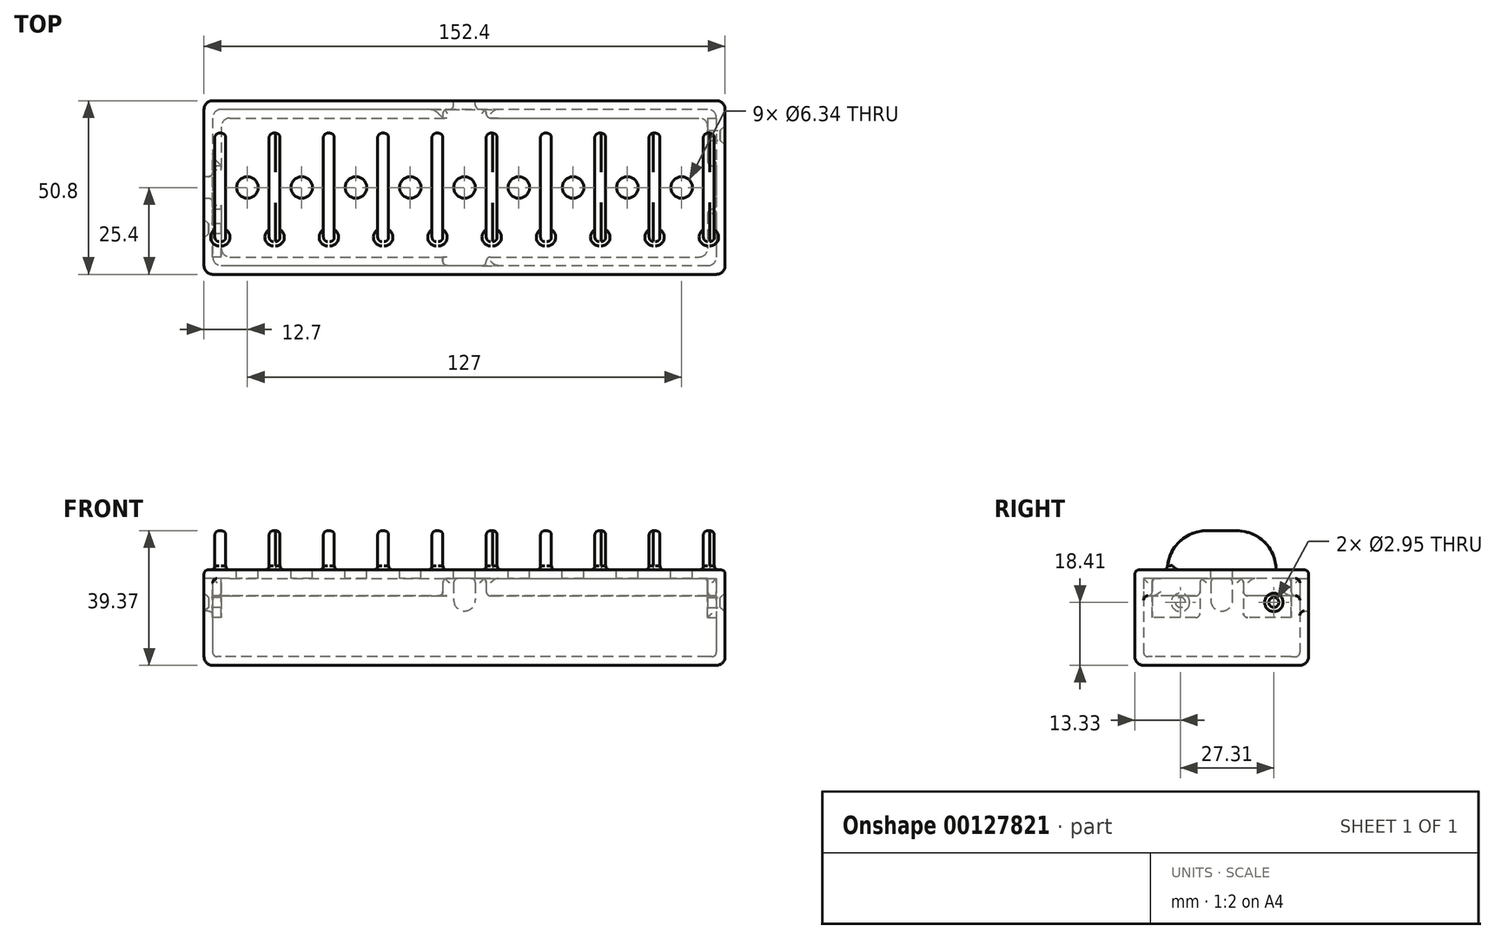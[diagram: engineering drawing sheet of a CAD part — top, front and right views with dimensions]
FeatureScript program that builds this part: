
annotation { "Feature Type Name" : "Feature", "Feature Type Description" : "" }
export const myFeature = defineFeature(function(context is Context, id is Id, definition is map)
    precondition{}
    {
        {
            var Q0;
            Q0=qCreatedBy(makeId("Top.planeOp"),FACE);
            var sketch = newSketch(context, id + "F0", { "sketchPlane" : qUnion([Q0])});
            skLineSegment(sketch, "E0.bottom", {"start": v(76.2, 25.4) * mm, "end": v(-76.2, 25.4) * mm});
            skLineSegment(sketch, "E0.top", {"start": v(76.2, -25.4) * mm, "end": v(-76.2, -25.4) * mm});
            skLineSegment(sketch, "E0.left", {"start": v(76.2, 25.4) * mm, "end": v(76.2, -25.4) * mm});
            skLineSegment(sketch, "E0.right", {"start": v(-76.2, 25.4) * mm, "end": v(-76.2, -25.4) * mm});
            skPoint(sketch, "E0.middle", {"position": v(0, 0) * mm});
            skSolve(sketch);
        }
        {
            var Q0;
            Q0=makeQuery(id+"F0.imprint","IMPRINT",FACE,{"disambiguationData":[TD([[makeQuery(id+"F0.imprint","IMPRINT",EDGE,{"derivedFrom":sQuery(id+"F0.wireOp",EDGE,"E0.bottom")}),1.0]])]});
            extrude(context, id + "F1", {"entities" : qUnion([Q0]), "depth" : 25.4 * mm});
        }
        {
            var Q0;
            Q0=makeQuery(id+"F1.opExtrude","CAP_FACE",FACE,{"disambiguationData":[OSD([sQuery(id+"F0.wireOp",EDGE,"E0.bottom"),sQuery(id+"F0.wireOp",EDGE,"E0.top"),sQuery(id+"F0.wireOp",EDGE,"E0.left"),sQuery(id+"F0.wireOp",EDGE,"E0.right")])],"isStart":false});
            shell(context, id + "F2", {"entities" : qUnion([Q0]), "thickness" : 2.54 * mm});
        }
        {
            var Q0;
            Q0=makeQuery(id+"F1.opExtrude","CAP_FACE",FACE,{"disambiguationData":[OSD([sQuery(id+"F0.wireOp",EDGE,"E0.bottom"),sQuery(id+"F0.wireOp",EDGE,"E0.top"),sQuery(id+"F0.wireOp",EDGE,"E0.left"),sQuery(id+"F0.wireOp",EDGE,"E0.right")])],"isStart":false});
            var sketch = newSketch(context, id + "F3", { "sketchPlane" : qUnion([Q0])});
            skLineSegment(sketch, "E1.bottom", {"start": v(-73.66, 22.86) * mm, "end": v(73.66, 22.86) * mm});
            skLineSegment(sketch, "E1.top", {"start": v(-73.66, -22.86) * mm, "end": v(73.66, -22.86) * mm});
            skLineSegment(sketch, "E1.left", {"start": v(-73.66, 22.86) * mm, "end": v(-73.66, -22.86) * mm});
            skLineSegment(sketch, "E1.right", {"start": v(73.66, 22.86) * mm, "end": v(73.66, -22.86) * mm});
            skLineSegment(sketch, "E2.0", {"start": v(-71.12, -20.32) * mm, "end": v(71.12, -20.32) * mm});
            skLineSegment(sketch, "E2.1", {"start": v(-71.12, 20.32) * mm, "end": v(-71.12, -20.32) * mm});
            skLineSegment(sketch, "E2.2", {"start": v(-71.12, 20.32) * mm, "end": v(71.12, 20.32) * mm});
            skLineSegment(sketch, "E2.3", {"start": v(71.12, 20.32) * mm, "end": v(71.12, -20.32) * mm});
            skSolve(sketch);
        }
        {
            var Q0;
            Q0 = qSketchRegion(id + "F3", true);
            extrude(context, id + "F4", {"entities" : qUnion([Q0]), "oppositeDirection" : true, "depth" : 5.08 * mm});
        }
        {
            var Q0;
            Q0=makeQuery(id+"F4.opExtrude","CAP_FACE",FACE,{"disambiguationData":[OSD([sQuery(id+"F3.wireOp",EDGE,"E1.bottom"),sQuery(id+"F3.wireOp",EDGE,"E1.top"),sQuery(id+"F3.wireOp",EDGE,"E1.left"),sQuery(id+"F3.wireOp",EDGE,"E1.right"),sQuery(id+"F3.wireOp",EDGE,"E2.0"),sQuery(id+"F3.wireOp",EDGE,"E2.1"),sQuery(id+"F3.wireOp",EDGE,"E2.2"),sQuery(id+"F3.wireOp",EDGE,"E2.3")])],"isStart":true});
            var sketch = newSketch(context, id + "F5", { "sketchPlane" : qUnion([Q0])});
            skLineSegment(sketch, "E3.0", {"start": v(76.2, -25.4) * mm, "end": v(-76.2, -25.4) * mm});
            skLineSegment(sketch, "E4.0", {"start": v(-76.2, 25.4) * mm, "end": v(-76.2, -25.4) * mm});
            skLineSegment(sketch, "E5.0", {"start": v(76.2, 25.4) * mm, "end": v(-76.2, 25.4) * mm});
            skLineSegment(sketch, "E6.0", {"start": v(76.2, 25.4) * mm, "end": v(76.2, -25.4) * mm});
            skSolve(sketch);
        }
        {
            var Q0;
            Q0 = qSketchRegion(id + "F5", true);
            extrude(context, id + "F6", {"entities" : qUnion([Q0]), "operationType" : NewBodyOperationType.ADD, "depth" : 2.54 * mm});
        }
        {
            var Q0;
            Q0=makeQuery(id+"F1.opExtrude","SWEPT_FACE",FACE,{"disambiguationData":[OSD([sQuery(id+"F0.wireOp",EDGE,"E0.bottom")])]});
            var sketch = newSketch(context, id + "F7", { "sketchPlane" : qUnion([Q0])});
            skLineSegment(sketch, "E7", {"start": v(-3.17, 25.4) * mm, "end": v(-3.17, 19.05) * mm});
            skLineSegment(sketch, "E8", {"start": v(-3.17, 25.4) * mm, "end": v(3.17, 25.4) * mm});
            skLineSegment(sketch, "E9", {"start": v(3.17, 25.4) * mm, "end": v(3.17, 19.05) * mm});
            skArc(sketch, "E10", {"start": v(-3.17, 19.05) * mm, "mid": v(0, 15.88) * mm, "end": v(3.17, 19.05) * mm});
            skSolve(sketch);
        }
        {
            var Q0;
            Q0=makeQuery(id+"F7.imprint","IMPRINT",FACE,{"disambiguationData":[TD([[makeQuery(id+"F7.imprint","IMPRINT",EDGE,{"derivedFrom":sQuery(id+"F7.wireOp",EDGE,"E7")}),1.0]])]});
            var Q1;
            Q1=makeQuery(id+"F2.opShell","OFFSET_FACE",FACE,{"disambiguationData":[OSD([sQuery(id+"F0.wireOp",EDGE,"E0.bottom")])]});
            extrude(context, id + "F8", {"entities" : qUnion([Q0]), "operationType" : NewBodyOperationType.REMOVE, "endBound" : BoundingType.UP_TO_SURFACE, "oppositeDirection" : true, "endBoundEntityFace" : qUnion([Q1]), "depth" : 6.35 * mm});
        }
        {
            var Q0;
            Q0=makeQuery(id+"F1.opExtrude","SWEPT_FACE",FACE,{"disambiguationData":[OSD([sQuery(id+"F0.wireOp",EDGE,"E0.right")])]});
            var sketch = newSketch(context, id + "F9", { "sketchPlane" : qUnion([Q0])});
            skLineSegment(sketch, "E11", {"start": v(-3.17, 19.05) * mm, "end": v(-3.17, 25.4) * mm});
            skLineSegment(sketch, "E12", {"start": v(-3.17, 25.4) * mm, "end": v(3.18, 25.4) * mm});
            skLineSegment(sketch, "E13", {"start": v(3.18, 25.4) * mm, "end": v(3.18, 19.05) * mm});
            skArc(sketch, "E14", {"start": v(-3.17, 19.05) * mm, "mid": v(0, 15.87) * mm, "end": v(3.18, 19.05) * mm});
            skSolve(sketch);
        }
        {
            var Q0;
            Q0=makeQuery(id+"F9.imprint","IMPRINT",FACE,{"disambiguationData":[TD([[makeQuery(id+"F9.imprint","IMPRINT",EDGE,{"derivedFrom":sQuery(id+"F9.wireOp",EDGE,"E11")}),-1.0]])]});
            var Q1;
            Q1=makeQuery(id+"F2.opShell","OFFSET_FACE",FACE,{"disambiguationData":[OSD([sQuery(id+"F0.wireOp",EDGE,"E0.right")])]});
            extrude(context, id + "F10", {"entities" : qUnion([Q0]), "operationType" : NewBodyOperationType.REMOVE, "endBound" : BoundingType.UP_TO_SURFACE, "oppositeDirection" : true, "endBoundEntityFace" : qUnion([Q1]), "depth" : 25.4 * mm});
        }
        {
            var Q0;
            Q0=makeQuery(id+"F4.opExtrude","CAP_FACE",FACE,{"disambiguationData":[OSD([sQuery(id+"F3.wireOp",EDGE,"E1.bottom"),sQuery(id+"F3.wireOp",EDGE,"E1.top"),sQuery(id+"F3.wireOp",EDGE,"E1.left"),sQuery(id+"F3.wireOp",EDGE,"E1.right"),sQuery(id+"F3.wireOp",EDGE,"E2.0"),sQuery(id+"F3.wireOp",EDGE,"E2.1"),sQuery(id+"F3.wireOp",EDGE,"E2.2"),sQuery(id+"F3.wireOp",EDGE,"E2.3")])],"isStart":false});
            var sketch = newSketch(context, id + "F11", { "sketchPlane" : qUnion([Q0])});
            skLineSegment(sketch, "E15.bottom", {"start": v(71.12, -6.35) * mm, "end": v(73.66, -6.35) * mm});
            skLineSegment(sketch, "E15.top", {"start": v(71.12, 6.35) * mm, "end": v(73.66, 6.35) * mm});
            skLineSegment(sketch, "E15.left", {"start": v(71.12, -6.35) * mm, "end": v(71.12, 6.35) * mm});
            skLineSegment(sketch, "E15.right", {"start": v(73.66, -6.35) * mm, "end": v(73.66, 6.35) * mm});
            skLineSegment(sketch, "E16.bottom", {"start": v(-6.35, 20.32) * mm, "end": v(6.35, 20.32) * mm});
            skLineSegment(sketch, "E16.top", {"start": v(-6.35, 22.86) * mm, "end": v(6.35, 22.86) * mm});
            skLineSegment(sketch, "E16.left", {"start": v(-6.35, 20.32) * mm, "end": v(-6.35, 22.86) * mm});
            skLineSegment(sketch, "E16.right", {"start": v(6.35, 20.32) * mm, "end": v(6.35, 22.86) * mm});
            skLineSegment(sketch, "E17.bottom", {"start": v(-71.12, -6.35) * mm, "end": v(-73.66, -6.35) * mm});
            skLineSegment(sketch, "E17.top", {"start": v(-71.12, 6.35) * mm, "end": v(-73.66, 6.35) * mm});
            skLineSegment(sketch, "E17.left", {"start": v(-71.12, -6.35) * mm, "end": v(-71.12, 6.35) * mm});
            skLineSegment(sketch, "E17.right", {"start": v(-73.66, -6.35) * mm, "end": v(-73.66, 6.35) * mm});
            skLineSegment(sketch, "E18.bottom", {"start": v(6.35, -22.86) * mm, "end": v(-6.35, -22.86) * mm});
            skLineSegment(sketch, "E18.top", {"start": v(6.35, -20.32) * mm, "end": v(-6.35, -20.32) * mm});
            skLineSegment(sketch, "E18.left", {"start": v(6.35, -22.86) * mm, "end": v(6.35, -20.32) * mm});
            skLineSegment(sketch, "E18.right", {"start": v(-6.35, -22.86) * mm, "end": v(-6.35, -20.32) * mm});
            skSolve(sketch);
        }
        {
            var Q0;
            Q0=makeQuery(id+"F11.imprint","IMPRINT",FACE,{"disambiguationData":[TD([[makeQuery(id+"F11.imprint","IMPRINT",EDGE,{"derivedFrom":sQuery(id+"F11.wireOp",EDGE,"E18.bottom")}),-1.0]])]});
            var Q1;
            Q1=makeQuery(id+"F11.imprint","IMPRINT",FACE,{"disambiguationData":[TD([[makeQuery(id+"F11.imprint","IMPRINT",EDGE,{"derivedFrom":sQuery(id+"F11.wireOp",EDGE,"E16.bottom")}),1.0]])]});
            var Q2;
            Q2=makeQuery(id+"F11.imprint","IMPRINT",FACE,{"disambiguationData":[TD([[makeQuery(id+"F11.imprint","IMPRINT",EDGE,{"derivedFrom":sQuery(id+"F11.wireOp",EDGE,"E15.bottom")}),1.0]])]});
            var Q3;
            Q3=makeQuery(id+"F11.imprint","IMPRINT",FACE,{"disambiguationData":[TD([[makeQuery(id+"F11.imprint","IMPRINT",EDGE,{"derivedFrom":sQuery(id+"F11.wireOp",EDGE,"E17.bottom")}),-1.0]])]});
            var Q4;
            {var subQ0=sQuery(id+"F5.wireOp",EDGE,"E5.0");var subQ1=sQuery(id+"F5.wireOp",EDGE,"E3.0");var subQ2=sQuery(id+"F5.wireOp",EDGE,"E4.0");var subQ3=sQuery(id+"F5.wireOp",EDGE,"E6.0");Q4=makeQuery(id+"F6.boolean.opBoolean","SPLIT",FACE,{"disambiguationData":[TD([makeQuery(id+"F4.opExtrude","SWEPT_FACE",FACE,{"disambiguationData":[OSD([sQuery(id+"F3.wireOp",EDGE,"E1.bottom")])]})])],"derivedFrom":makeQuery(id+"F6.opExtrude","CAP_FACE",FACE,{"disambiguationData":[OSD([subQ1,subQ2,subQ0,subQ3])],"isStart":true})});}
            extrude(context, id + "F12", {"entities" : qUnion([Q0, Q1, Q2, Q3]), "operationType" : NewBodyOperationType.REMOVE, "endBound" : BoundingType.UP_TO_SURFACE, "oppositeDirection" : true, "endBoundEntityFace" : qUnion([Q4]), "depth" : 25.4 * mm});
        }
        {
            var Q0;
            Q0=makeQuery(id+"F1.opExtrude","SWEPT_EDGE",EDGE,{"disambiguationData":[OSD([sQuery(id+"F0.wireOp",EDGE,"E0.bottom"),sQuery(id+"F0.wireOp",EDGE,"E0.right")])]});
            var Q1;
            Q1=makeQuery(id+"F1.opExtrude","SWEPT_EDGE",EDGE,{"disambiguationData":[OSD([sQuery(id+"F0.wireOp",EDGE,"E0.top"),sQuery(id+"F0.wireOp",EDGE,"E0.right")])]});
            var Q2;
            Q2=makeQuery(id+"F1.opExtrude","SWEPT_EDGE",EDGE,{"disambiguationData":[OSD([sQuery(id+"F0.wireOp",EDGE,"E0.top"),sQuery(id+"F0.wireOp",EDGE,"E0.left")])]});
            var Q3;
            Q3=makeQuery(id+"F1.opExtrude","SWEPT_EDGE",EDGE,{"disambiguationData":[OSD([sQuery(id+"F0.wireOp",EDGE,"E0.bottom"),sQuery(id+"F0.wireOp",EDGE,"E0.left")])]});
            var Q4;
            Q4=makeQuery(id+"F2.opShell","OFFSET_EDGE",EDGE,{"disambiguationData":[OSD([sQuery(id+"F0.wireOp",EDGE,"E0.top"),sQuery(id+"F0.wireOp",EDGE,"E0.left")])]});
            var Q5;
            Q5=makeQuery(id+"F2.opShell","OFFSET_EDGE",EDGE,{"disambiguationData":[OSD([sQuery(id+"F0.wireOp",EDGE,"E0.bottom"),sQuery(id+"F0.wireOp",EDGE,"E0.left")])]});
            var Q6;
            Q6=makeQuery(id+"F2.opShell","OFFSET_EDGE",EDGE,{"disambiguationData":[OSD([sQuery(id+"F0.wireOp",EDGE,"E0.top"),sQuery(id+"F0.wireOp",EDGE,"E0.right")])]});
            var Q7;
            Q7=makeQuery(id+"F2.opShell","OFFSET_EDGE",EDGE,{"disambiguationData":[OSD([sQuery(id+"F0.wireOp",EDGE,"E0.bottom"),sQuery(id+"F0.wireOp",EDGE,"E0.right")])]});
            fillet(context, id + "F13", {"entities" : qUnion([Q0, Q1, Q2, Q3, Q4, Q5, Q6, Q7]), "radius" : 2.54 * mm, "tangentPropagation" : true, "allowEdgeOverflow" : false});
        }
        {
            var Q0;
            Q0=makeQuery(id+"F6.opExtrude","SWEPT_EDGE",EDGE,{"disambiguationData":[OSD([sQuery(id+"F5.wireOp",EDGE,"E5.0"),sQuery(id+"F5.wireOp",EDGE,"E6.0")])]});
            var Q1;
            Q1=makeQuery(id+"F6.opExtrude","SWEPT_EDGE",EDGE,{"disambiguationData":[OSD([sQuery(id+"F5.wireOp",EDGE,"E3.0"),sQuery(id+"F5.wireOp",EDGE,"E6.0")])]});
            var Q2;
            Q2=makeQuery(id+"F4.opExtrude","SWEPT_EDGE",EDGE,{"disambiguationData":[OSD([sQuery(id+"F3.wireOp",EDGE,"E1.bottom"),sQuery(id+"F3.wireOp",EDGE,"E1.right")])]});
            var Q3;
            Q3=makeQuery(id+"F4.opExtrude","SWEPT_EDGE",EDGE,{"disambiguationData":[OSD([sQuery(id+"F3.wireOp",EDGE,"E1.top"),sQuery(id+"F3.wireOp",EDGE,"E1.right")])]});
            var Q4;
            Q4=makeQuery(id+"F4.opExtrude","SWEPT_EDGE",EDGE,{"disambiguationData":[OSD([sQuery(id+"F3.wireOp",EDGE,"E2.2"),sQuery(id+"F3.wireOp",EDGE,"E2.3")])]});
            var Q5;
            Q5=makeQuery(id+"F4.opExtrude","SWEPT_EDGE",EDGE,{"disambiguationData":[OSD([sQuery(id+"F3.wireOp",EDGE,"E2.0"),sQuery(id+"F3.wireOp",EDGE,"E2.3")])]});
            var Q6;
            Q6=makeQuery(id+"F4.opExtrude","SWEPT_EDGE",EDGE,{"disambiguationData":[OSD([sQuery(id+"F3.wireOp",EDGE,"E1.bottom"),sQuery(id+"F3.wireOp",EDGE,"E1.left")])]});
            var Q7;
            Q7=makeQuery(id+"F6.opExtrude","SWEPT_EDGE",EDGE,{"disambiguationData":[OSD([sQuery(id+"F5.wireOp",EDGE,"E4.0"),sQuery(id+"F5.wireOp",EDGE,"E5.0")])]});
            var Q8;
            Q8=makeQuery(id+"F6.opExtrude","SWEPT_EDGE",EDGE,{"disambiguationData":[OSD([sQuery(id+"F5.wireOp",EDGE,"E3.0"),sQuery(id+"F5.wireOp",EDGE,"E4.0")])]});
            var Q9;
            Q9=makeQuery(id+"F4.opExtrude","SWEPT_EDGE",EDGE,{"disambiguationData":[OSD([sQuery(id+"F3.wireOp",EDGE,"E1.top"),sQuery(id+"F3.wireOp",EDGE,"E1.left")])]});
            var Q10;
            Q10=makeQuery(id+"F4.opExtrude","SWEPT_EDGE",EDGE,{"disambiguationData":[OSD([sQuery(id+"F3.wireOp",EDGE,"E2.0"),sQuery(id+"F3.wireOp",EDGE,"E2.1")])]});
            var Q11;
            Q11=makeQuery(id+"F4.opExtrude","SWEPT_EDGE",EDGE,{"disambiguationData":[OSD([sQuery(id+"F3.wireOp",EDGE,"E2.1"),sQuery(id+"F3.wireOp",EDGE,"E2.2")])]});
            fillet(context, id + "F14", {"entities" : qUnion([Q0, Q1, Q2, Q3, Q4, Q5, Q6, Q7, Q8, Q9, Q10, Q11]), "radius" : 2.54 * mm, "tangentPropagation" : true, "allowEdgeOverflow" : false});
        }
        {
            var Q0;
            Q0=makeQuery(id+"F1.opExtrude","CAP_FACE",FACE,{"disambiguationData":[OSD([sQuery(id+"F0.wireOp",EDGE,"E0.bottom"),sQuery(id+"F0.wireOp",EDGE,"E0.top"),sQuery(id+"F0.wireOp",EDGE,"E0.left"),sQuery(id+"F0.wireOp",EDGE,"E0.right")])],"isStart":true});
            fillet(context, id + "F15", {"entities" : qUnion([Q0]), "radius" : 2.54 * mm, "tangentPropagation" : true, "allowEdgeOverflow" : false});
        }
        {
            var Q0;
            Q0=makeQuery(id+"F6.opExtrude","CAP_FACE",FACE,{"disambiguationData":[OSD([sQuery(id+"F5.wireOp",EDGE,"E3.0"),sQuery(id+"F5.wireOp",EDGE,"E4.0"),sQuery(id+"F5.wireOp",EDGE,"E5.0"),sQuery(id+"F5.wireOp",EDGE,"E6.0")])],"isStart":false});
            var sketch = newSketch(context, id + "F16", { "sketchPlane" : qUnion([Q0])});
            skCircle(sketch, "E19", {"center": v(63.5, 0) * mm, "radius": 3.17 * mm});
            skCircle(sketch, "E20.1.0.0", {"center": v(47.62, 0) * mm, "radius": 3.17 * mm});
            skCircle(sketch, "E20.2.0.0", {"center": v(31.75, 0) * mm, "radius": 3.17 * mm});
            skCircle(sketch, "E20.3.0.0", {"center": v(15.88, 0) * mm, "radius": 3.17 * mm});
            skCircle(sketch, "E20.4.0.0", {"center": v(0, 0) * mm, "radius": 3.17 * mm});
            skCircle(sketch, "E20.5.0.0", {"center": v(-15.87, 0) * mm, "radius": 3.17 * mm});
            skLineSegment(sketch, "E20.direction1", {"start": v(63.5, 0) * mm, "end": v(47.62, 0) * mm, "construction": true});
            skCircle(sketch, "E21.0.6.0", {"center": v(-31.75, 0) * mm, "radius": 3.17 * mm});
            skCircle(sketch, "E21.0.7.0", {"center": v(-47.62, 0) * mm, "radius": 3.17 * mm});
            skCircle(sketch, "E22.0.8.0", {"center": v(-63.5, 0) * mm, "radius": 3.17 * mm});
            skSolve(sketch);
        }
        {
            var Q0;
            Q0 = qSketchRegion(id + "F16", true);
            var Q1;
            {var subQ0=sQuery(id+"F5.wireOp",EDGE,"E6.0");var subQ1=sQuery(id+"F5.wireOp",EDGE,"E5.0");var subQ2=sQuery(id+"F5.wireOp",EDGE,"E4.0");var subQ3=sQuery(id+"F5.wireOp",EDGE,"E3.0");var subQ4=makeQuery(id+"F6.opExtrude","CAP_FACE",FACE,{"disambiguationData":[OSD([subQ3,subQ2,subQ1,subQ0])],"isStart":true});Q1=makeQuery(id+"F12.boolean.opBoolean","MERGE",FACE,{"derivedFrom":[makeQuery(id+"F6.boolean.opBoolean","SPLIT",FACE,{"disambiguationData":[TD([makeQuery(id+"F4.opExtrude","SWEPT_FACE",FACE,{"disambiguationData":[OSD([sQuery(id+"F3.wireOp",EDGE,"E1.bottom")])]})])],"derivedFrom":subQ4}),makeQuery(id+"F6.boolean.opBoolean","SPLIT",FACE,{"disambiguationData":[TD([makeQuery(id+"F4.opExtrude","SWEPT_FACE",FACE,{"disambiguationData":[OSD([sQuery(id+"F3.wireOp",EDGE,"E2.0")])]})])],"derivedFrom":subQ4})],"fromTools":[makeQuery(id+"F12.opExtrude","CAP_FACE",FACE,{"disambiguationData":[OSD([sQuery(id+"F11.wireOp",EDGE,"E15.bottom"),sQuery(id+"F11.wireOp",EDGE,"E15.top"),sQuery(id+"F11.wireOp",EDGE,"E15.left"),sQuery(id+"F11.wireOp",EDGE,"E15.right")])],"isStart":false}),makeQuery(id+"F12.opExtrude","CAP_FACE",FACE,{"disambiguationData":[OSD([sQuery(id+"F11.wireOp",EDGE,"E16.bottom"),sQuery(id+"F11.wireOp",EDGE,"E16.top"),sQuery(id+"F11.wireOp",EDGE,"E16.left"),sQuery(id+"F11.wireOp",EDGE,"E16.right")])],"isStart":false}),makeQuery(id+"F12.opExtrude","CAP_FACE",FACE,{"disambiguationData":[OSD([sQuery(id+"F11.wireOp",EDGE,"E17.bottom"),sQuery(id+"F11.wireOp",EDGE,"E17.top"),sQuery(id+"F11.wireOp",EDGE,"E17.left"),sQuery(id+"F11.wireOp",EDGE,"E17.right")])],"isStart":false}),makeQuery(id+"F12.opExtrude","CAP_FACE",FACE,{"disambiguationData":[OSD([sQuery(id+"F11.wireOp",EDGE,"E18.bottom"),sQuery(id+"F11.wireOp",EDGE,"E18.top"),sQuery(id+"F11.wireOp",EDGE,"E18.left"),sQuery(id+"F11.wireOp",EDGE,"E18.right")])],"isStart":false})]});}
            extrude(context, id + "F17", {"entities" : qUnion([Q0]), "operationType" : NewBodyOperationType.REMOVE, "endBound" : BoundingType.UP_TO_SURFACE, "oppositeDirection" : true, "endBoundEntityFace" : qUnion([Q1]), "depth" : 25.4 * mm});
        }
        {
            var Q0;
            {var subQ0=sQuery(id+"F3.wireOp",EDGE,"E2.3");var subQ1=sQuery(id+"F3.wireOp",EDGE,"E2.2");var subQ2=sQuery(id+"F3.wireOp",EDGE,"E1.right");var subQ3=sQuery(id+"F3.wireOp",EDGE,"E1.bottom");Q0=makeQuery(id+"F12.boolean.opBoolean","SPLIT",FACE,{"disambiguationData":[TD([makeQuery(id+"F12.opExtrude","SWEPT_FACE",FACE,{"disambiguationData":[OSD([sQuery(id+"F11.wireOp",EDGE,"E15.bottom")])]})])],"derivedFrom":makeQuery(id+"F4.opExtrude","CAP_FACE",FACE,{"disambiguationData":[OSD([subQ3,sQuery(id+"F3.wireOp",EDGE,"E1.top"),sQuery(id+"F3.wireOp",EDGE,"E1.left"),subQ2,sQuery(id+"F3.wireOp",EDGE,"E2.0"),sQuery(id+"F3.wireOp",EDGE,"E2.1"),subQ1,subQ0])],"isStart":false})});}
            var sketch = newSketch(context, id + "F18", { "sketchPlane" : qUnion([Q0])});
            skLineSegment(sketch, "E23.bottom", {"start": v(73.66, -6.35) * mm, "end": v(71.12, -6.35) * mm});
            skLineSegment(sketch, "E23.left", {"start": v(73.66, -6.35) * mm, "end": v(73.66, -20.32) * mm});
            skLineSegment(sketch, "E24.top", {"start": v(-71.12, 6.35) * mm, "end": v(-73.66, 6.35) * mm});
            skLineSegment(sketch, "E24.right", {"start": v(-73.66, 20.32) * mm, "end": v(-73.66, 6.35) * mm});
            skLineSegment(sketch, "E25", {"start": v(71.12, -6.35) * mm, "end": v(71.12, -20.32) * mm});
            skLineSegment(sketch, "E26", {"start": v(71.12, -20.32) * mm, "end": v(73.66, -20.32) * mm});
            skLineSegment(sketch, "E27", {"start": v(-71.12, 6.35) * mm, "end": v(-71.12, 20.32) * mm});
            skLineSegment(sketch, "E28", {"start": v(-71.12, 20.32) * mm, "end": v(-73.66, 20.32) * mm});
            skSolve(sketch);
        }
        {
            var Q0;
            Q0=makeQuery(id+"F18.imprint","IMPRINT",FACE,{"disambiguationData":[TD([[makeQuery(id+"F18.imprint","IMPRINT",EDGE,{"derivedFrom":sQuery(id+"F18.wireOp",EDGE,"E23.bottom")}),-1.0]])]});
            var Q1;
            Q1=makeQuery(id+"F18.imprint","IMPRINT",FACE,{"disambiguationData":[TD([[makeQuery(id+"F18.imprint","IMPRINT",EDGE,{"derivedFrom":sQuery(id+"F18.wireOp",EDGE,"E24.bottom")}),1.0]])]});
            var Q2;
            Q2=makeQuery(id+"F18.imprint","IMPRINT",FACE,{"disambiguationData":[TD([[makeQuery(id+"F18.imprint","IMPRINT",EDGE,{"derivedFrom":sQuery(id+"F18.wireOp",EDGE,"E24.top")}),-1.0]])]});
            extrude(context, id + "F19", {"entities" : qUnion([Q0, Q1, Q2]), "operationType" : NewBodyOperationType.ADD, "depth" : 6.35 * mm});
        }
        {
            var Q0;
            Q0=makeQuery(id+"F6.opExtrude","CAP_EDGE",EDGE,{"disambiguationData":[OSD([sQuery(id+"F5.wireOp",EDGE,"E6.0")])],"isStart":false});
            var Q1;
            Q1=makeQuery(id+"F6.opExtrude","CAP_EDGE",EDGE,{"disambiguationData":[OSD([sQuery(id+"F5.wireOp",EDGE,"E6.0")])],"isStart":true});
            var Q2;
            Q2=makeQuery(id+"F17.boolean.opBoolean","COPY",EDGE,{"derivedFrom":makeQuery(id+"F17.opExtrude","CAP_EDGE",EDGE,{"disambiguationData":[OSD([sQuery(id+"F16.wireOp",EDGE,"E19")])],"isStart":true})});
            var Q3;
            Q3=makeQuery(id+"F17.boolean.opBoolean","COPY",EDGE,{"derivedFrom":makeQuery(id+"F17.opExtrude","CAP_EDGE",EDGE,{"disambiguationData":[OSD([sQuery(id+"F16.wireOp",EDGE,"E20.1.0.0")])],"isStart":true})});
            var Q4;
            Q4=makeQuery(id+"F17.boolean.opBoolean","COPY",EDGE,{"derivedFrom":makeQuery(id+"F17.opExtrude","CAP_EDGE",EDGE,{"disambiguationData":[OSD([sQuery(id+"F16.wireOp",EDGE,"E20.2.0.0")])],"isStart":true})});
            var Q5;
            Q5=makeQuery(id+"F17.boolean.opBoolean","COPY",EDGE,{"derivedFrom":makeQuery(id+"F17.opExtrude","CAP_EDGE",EDGE,{"disambiguationData":[OSD([sQuery(id+"F16.wireOp",EDGE,"E20.3.0.0")])],"isStart":true})});
            var Q6;
            Q6=makeQuery(id+"F17.boolean.opBoolean","COPY",EDGE,{"derivedFrom":makeQuery(id+"F17.opExtrude","CAP_EDGE",EDGE,{"disambiguationData":[OSD([sQuery(id+"F16.wireOp",EDGE,"E20.4.0.0")])],"isStart":true})});
            var Q7;
            Q7=makeQuery(id+"F17.boolean.opBoolean","COPY",EDGE,{"derivedFrom":makeQuery(id+"F17.opExtrude","CAP_EDGE",EDGE,{"disambiguationData":[OSD([sQuery(id+"F16.wireOp",EDGE,"E20.5.0.0")])],"isStart":true})});
            var Q8;
            Q8=makeQuery(id+"F17.boolean.opBoolean","COPY",EDGE,{"derivedFrom":makeQuery(id+"F17.opExtrude","CAP_EDGE",EDGE,{"disambiguationData":[OSD([sQuery(id+"F16.wireOp",EDGE,"E21.0.6.0")])],"isStart":true})});
            var Q9;
            Q9=makeQuery(id+"F17.boolean.opBoolean","COPY",EDGE,{"derivedFrom":makeQuery(id+"F17.opExtrude","CAP_EDGE",EDGE,{"disambiguationData":[OSD([sQuery(id+"F16.wireOp",EDGE,"E21.0.7.0")])],"isStart":true})});
            var Q10;
            Q10=makeQuery(id+"F17.boolean.opBoolean","COPY",EDGE,{"derivedFrom":makeQuery(id+"F17.opExtrude","CAP_EDGE",EDGE,{"disambiguationData":[OSD([sQuery(id+"F16.wireOp",EDGE,"E22.0.8.0")])],"isStart":true})});
            var Q11;
            {var subQ0=sQuery(id+"F5.wireOp",EDGE,"E6.0");var subQ1=sQuery(id+"F5.wireOp",EDGE,"E5.0");var subQ2=sQuery(id+"F5.wireOp",EDGE,"E4.0");var subQ3=sQuery(id+"F5.wireOp",EDGE,"E3.0");var subQ4=makeQuery(id+"F6.opExtrude","CAP_FACE",FACE,{"disambiguationData":[OSD([subQ3,subQ2,subQ1,subQ0])],"isStart":true});var subQ5=sQuery(id+"F3.wireOp",EDGE,"E1.top");var subQ6=sQuery(id+"F3.wireOp",EDGE,"E1.right");Q11=makeQuery(id+"F14.opFillet","BLEND_EDGE",EDGE,{"blendedFrom":[makeQuery(id+"F4.opExtrude","SWEPT_EDGE",EDGE,{"disambiguationData":[OSD([subQ5,subQ6])]}),makeQuery(id+"F12.boolean.opBoolean","MERGE",FACE,{"derivedFrom":[makeQuery(id+"F6.boolean.opBoolean","SPLIT",FACE,{"disambiguationData":[TD([makeQuery(id+"F4.opExtrude","SWEPT_FACE",FACE,{"disambiguationData":[OSD([sQuery(id+"F3.wireOp",EDGE,"E1.bottom")])]})])],"derivedFrom":subQ4}),makeQuery(id+"F6.boolean.opBoolean","SPLIT",FACE,{"disambiguationData":[TD([makeQuery(id+"F4.opExtrude","SWEPT_FACE",FACE,{"disambiguationData":[OSD([sQuery(id+"F3.wireOp",EDGE,"E2.0")])]})])],"derivedFrom":subQ4})],"fromTools":[makeQuery(id+"F12.opExtrude","CAP_FACE",FACE,{"disambiguationData":[OSD([sQuery(id+"F11.wireOp",EDGE,"E15.bottom"),sQuery(id+"F11.wireOp",EDGE,"E15.top"),sQuery(id+"F11.wireOp",EDGE,"E15.left"),sQuery(id+"F11.wireOp",EDGE,"E15.right")])],"isStart":false}),makeQuery(id+"F12.opExtrude","CAP_FACE",FACE,{"disambiguationData":[OSD([sQuery(id+"F11.wireOp",EDGE,"E16.bottom"),sQuery(id+"F11.wireOp",EDGE,"E16.top"),sQuery(id+"F11.wireOp",EDGE,"E16.left"),sQuery(id+"F11.wireOp",EDGE,"E16.right")])],"isStart":false}),makeQuery(id+"F12.opExtrude","CAP_FACE",FACE,{"disambiguationData":[OSD([sQuery(id+"F11.wireOp",EDGE,"E17.bottom"),sQuery(id+"F11.wireOp",EDGE,"E17.top"),sQuery(id+"F11.wireOp",EDGE,"E17.left"),sQuery(id+"F11.wireOp",EDGE,"E17.right")])],"isStart":false}),makeQuery(id+"F12.opExtrude","CAP_FACE",FACE,{"disambiguationData":[OSD([sQuery(id+"F11.wireOp",EDGE,"E18.bottom"),sQuery(id+"F11.wireOp",EDGE,"E18.top"),sQuery(id+"F11.wireOp",EDGE,"E18.left"),sQuery(id+"F11.wireOp",EDGE,"E18.right")])],"isStart":false})]})],"blendedInto":[makeQuery(id+"F12.boolean.opBoolean","MERGE",FACE,{"derivedFrom":[makeQuery(id+"F6.boolean.opBoolean","SPLIT",FACE,{"disambiguationData":[TD([makeQuery(id+"F4.opExtrude","SWEPT_FACE",FACE,{"disambiguationData":[OSD([sQuery(id+"F3.wireOp",EDGE,"E1.bottom")])]})])],"derivedFrom":subQ4}),makeQuery(id+"F6.boolean.opBoolean","SPLIT",FACE,{"disambiguationData":[TD([makeQuery(id+"F4.opExtrude","SWEPT_FACE",FACE,{"disambiguationData":[OSD([sQuery(id+"F3.wireOp",EDGE,"E2.0")])]})])],"derivedFrom":subQ4})],"fromTools":[makeQuery(id+"F12.opExtrude","CAP_FACE",FACE,{"disambiguationData":[OSD([sQuery(id+"F11.wireOp",EDGE,"E15.bottom"),sQuery(id+"F11.wireOp",EDGE,"E15.top"),sQuery(id+"F11.wireOp",EDGE,"E15.left"),sQuery(id+"F11.wireOp",EDGE,"E15.right")])],"isStart":false}),makeQuery(id+"F12.opExtrude","CAP_FACE",FACE,{"disambiguationData":[OSD([sQuery(id+"F11.wireOp",EDGE,"E16.bottom"),sQuery(id+"F11.wireOp",EDGE,"E16.top"),sQuery(id+"F11.wireOp",EDGE,"E16.left"),sQuery(id+"F11.wireOp",EDGE,"E16.right")])],"isStart":false}),makeQuery(id+"F12.opExtrude","CAP_FACE",FACE,{"disambiguationData":[OSD([sQuery(id+"F11.wireOp",EDGE,"E17.bottom"),sQuery(id+"F11.wireOp",EDGE,"E17.top"),sQuery(id+"F11.wireOp",EDGE,"E17.left"),sQuery(id+"F11.wireOp",EDGE,"E17.right")])],"isStart":false}),makeQuery(id+"F12.opExtrude","CAP_FACE",FACE,{"disambiguationData":[OSD([sQuery(id+"F11.wireOp",EDGE,"E18.bottom"),sQuery(id+"F11.wireOp",EDGE,"E18.top"),sQuery(id+"F11.wireOp",EDGE,"E18.left"),sQuery(id+"F11.wireOp",EDGE,"E18.right")])],"isStart":false})]})]});}
            var Q12;
            {var subQ0=sQuery(id+"F3.wireOp",EDGE,"E1.right");var subQ1=sQuery(id+"F3.wireOp",EDGE,"E1.top");Q12=makeQuery(id+"F12.boolean.opBoolean","SPLIT",EDGE,{"disambiguationData":[TD([makeQuery(id+"F4.opExtrude","SWEPT_FACE",FACE,{"disambiguationData":[OSD([subQ1])]})])],"derivedFrom":makeQuery(id+"F4.opExtrude","CAP_EDGE",EDGE,{"disambiguationData":[OSD([subQ0])],"isStart":false})});}
            var Q13;
            {var subQ0=sQuery(id+"F3.wireOp",EDGE,"E2.3");var subQ1=sQuery(id+"F3.wireOp",EDGE,"E2.0");Q13=makeQuery(id+"F12.boolean.opBoolean","SPLIT",EDGE,{"disambiguationData":[TD([makeQuery(id+"F4.opExtrude","SWEPT_FACE",FACE,{"disambiguationData":[OSD([subQ1])]})])],"derivedFrom":makeQuery(id+"F4.opExtrude","CAP_EDGE",EDGE,{"disambiguationData":[OSD([subQ0])],"isStart":false})});}
            var Q14;
            {var subQ0=sQuery(id+"F3.wireOp",EDGE,"E2.0");var subQ1=sQuery(id+"F3.wireOp",EDGE,"E2.3");var subQ2=sQuery(id+"F5.wireOp",EDGE,"E6.0");var subQ3=sQuery(id+"F5.wireOp",EDGE,"E5.0");var subQ4=sQuery(id+"F5.wireOp",EDGE,"E4.0");var subQ5=sQuery(id+"F5.wireOp",EDGE,"E3.0");var subQ6=makeQuery(id+"F6.opExtrude","CAP_FACE",FACE,{"disambiguationData":[OSD([subQ5,subQ4,subQ3,subQ2])],"isStart":true});Q14=makeQuery(id+"F14.opFillet","BLEND_EDGE",EDGE,{"blendedFrom":[makeQuery(id+"F4.opExtrude","SWEPT_EDGE",EDGE,{"disambiguationData":[OSD([subQ0,subQ1])]}),makeQuery(id+"F12.boolean.opBoolean","MERGE",FACE,{"derivedFrom":[makeQuery(id+"F6.boolean.opBoolean","SPLIT",FACE,{"disambiguationData":[TD([makeQuery(id+"F4.opExtrude","SWEPT_FACE",FACE,{"disambiguationData":[OSD([sQuery(id+"F3.wireOp",EDGE,"E1.bottom")])]})])],"derivedFrom":subQ6}),makeQuery(id+"F6.boolean.opBoolean","SPLIT",FACE,{"disambiguationData":[TD([makeQuery(id+"F4.opExtrude","SWEPT_FACE",FACE,{"disambiguationData":[OSD([subQ0])]})])],"derivedFrom":subQ6})],"fromTools":[makeQuery(id+"F12.opExtrude","CAP_FACE",FACE,{"disambiguationData":[OSD([sQuery(id+"F11.wireOp",EDGE,"E15.bottom"),sQuery(id+"F11.wireOp",EDGE,"E15.top"),sQuery(id+"F11.wireOp",EDGE,"E15.left"),sQuery(id+"F11.wireOp",EDGE,"E15.right")])],"isStart":false}),makeQuery(id+"F12.opExtrude","CAP_FACE",FACE,{"disambiguationData":[OSD([sQuery(id+"F11.wireOp",EDGE,"E16.bottom"),sQuery(id+"F11.wireOp",EDGE,"E16.top"),sQuery(id+"F11.wireOp",EDGE,"E16.left"),sQuery(id+"F11.wireOp",EDGE,"E16.right")])],"isStart":false}),makeQuery(id+"F12.opExtrude","CAP_FACE",FACE,{"disambiguationData":[OSD([sQuery(id+"F11.wireOp",EDGE,"E17.bottom"),sQuery(id+"F11.wireOp",EDGE,"E17.top"),sQuery(id+"F11.wireOp",EDGE,"E17.left"),sQuery(id+"F11.wireOp",EDGE,"E17.right")])],"isStart":false}),makeQuery(id+"F12.opExtrude","CAP_FACE",FACE,{"disambiguationData":[OSD([sQuery(id+"F11.wireOp",EDGE,"E18.bottom"),sQuery(id+"F11.wireOp",EDGE,"E18.top"),sQuery(id+"F11.wireOp",EDGE,"E18.left"),sQuery(id+"F11.wireOp",EDGE,"E18.right")])],"isStart":false})]})],"blendedInto":[makeQuery(id+"F12.boolean.opBoolean","MERGE",FACE,{"derivedFrom":[makeQuery(id+"F6.boolean.opBoolean","SPLIT",FACE,{"disambiguationData":[TD([makeQuery(id+"F4.opExtrude","SWEPT_FACE",FACE,{"disambiguationData":[OSD([sQuery(id+"F3.wireOp",EDGE,"E1.bottom")])]})])],"derivedFrom":subQ6}),makeQuery(id+"F6.boolean.opBoolean","SPLIT",FACE,{"disambiguationData":[TD([makeQuery(id+"F4.opExtrude","SWEPT_FACE",FACE,{"disambiguationData":[OSD([subQ0])]})])],"derivedFrom":subQ6})],"fromTools":[makeQuery(id+"F12.opExtrude","CAP_FACE",FACE,{"disambiguationData":[OSD([sQuery(id+"F11.wireOp",EDGE,"E15.bottom"),sQuery(id+"F11.wireOp",EDGE,"E15.top"),sQuery(id+"F11.wireOp",EDGE,"E15.left"),sQuery(id+"F11.wireOp",EDGE,"E15.right")])],"isStart":false}),makeQuery(id+"F12.opExtrude","CAP_FACE",FACE,{"disambiguationData":[OSD([sQuery(id+"F11.wireOp",EDGE,"E16.bottom"),sQuery(id+"F11.wireOp",EDGE,"E16.top"),sQuery(id+"F11.wireOp",EDGE,"E16.left"),sQuery(id+"F11.wireOp",EDGE,"E16.right")])],"isStart":false}),makeQuery(id+"F12.opExtrude","CAP_FACE",FACE,{"disambiguationData":[OSD([sQuery(id+"F11.wireOp",EDGE,"E17.bottom"),sQuery(id+"F11.wireOp",EDGE,"E17.top"),sQuery(id+"F11.wireOp",EDGE,"E17.left"),sQuery(id+"F11.wireOp",EDGE,"E17.right")])],"isStart":false}),makeQuery(id+"F12.opExtrude","CAP_FACE",FACE,{"disambiguationData":[OSD([sQuery(id+"F11.wireOp",EDGE,"E18.bottom"),sQuery(id+"F11.wireOp",EDGE,"E18.top"),sQuery(id+"F11.wireOp",EDGE,"E18.left"),sQuery(id+"F11.wireOp",EDGE,"E18.right")])],"isStart":false})]})]});}
            var Q15;
            Q15=makeQuery(id+"F12.boolean.opBoolean","COPY",EDGE,{"derivedFrom":makeQuery(id+"F12.opExtrude","CAP_EDGE",EDGE,{"disambiguationData":[OSD([sQuery(id+"F11.wireOp",EDGE,"E16.right")])],"isStart":false})});
            var Q16;
            Q16=makeQuery(id+"F12.boolean.opBoolean","COPY",EDGE,{"derivedFrom":makeQuery(id+"F12.opExtrude","SWEPT_EDGE",EDGE,{"disambiguationData":[OSD([sQuery(id+"F3.wireOp",EDGE,"E2.0"),sQuery(id+"F11.wireOp",EDGE,"E16.bottom"),sQuery(id+"F11.wireOp",EDGE,"E16.right")])]})});
            var Q17;
            Q17=makeQuery(id+"F12.boolean.opBoolean","COPY",EDGE,{"derivedFrom":makeQuery(id+"F12.opExtrude","SWEPT_EDGE",EDGE,{"disambiguationData":[OSD([sQuery(id+"F3.wireOp",EDGE,"E1.top"),sQuery(id+"F11.wireOp",EDGE,"E16.top"),sQuery(id+"F11.wireOp",EDGE,"E16.right")])]})});
            var Q18;
            Q18=makeQuery(id+"F12.boolean.opBoolean","COPY",EDGE,{"derivedFrom":makeQuery(id+"F12.opExtrude","CAP_EDGE",EDGE,{"disambiguationData":[OSD([sQuery(id+"F11.wireOp",EDGE,"E16.right")])],"isStart":true})});
            var Q19;
            Q19=makeQuery(id+"F12.boolean.opBoolean","COPY",EDGE,{"derivedFrom":makeQuery(id+"F12.opExtrude","SWEPT_EDGE",EDGE,{"disambiguationData":[OSD([sQuery(id+"F3.wireOp",EDGE,"E2.0"),sQuery(id+"F11.wireOp",EDGE,"E16.bottom"),sQuery(id+"F11.wireOp",EDGE,"E16.left")])]})});
            var Q20;
            Q20=makeQuery(id+"F12.boolean.opBoolean","COPY",EDGE,{"derivedFrom":makeQuery(id+"F12.opExtrude","CAP_EDGE",EDGE,{"disambiguationData":[OSD([sQuery(id+"F11.wireOp",EDGE,"E16.left")])],"isStart":true})});
            var Q21;
            Q21=makeQuery(id+"F12.boolean.opBoolean","COPY",EDGE,{"derivedFrom":makeQuery(id+"F12.opExtrude","SWEPT_EDGE",EDGE,{"disambiguationData":[OSD([sQuery(id+"F3.wireOp",EDGE,"E1.top"),sQuery(id+"F11.wireOp",EDGE,"E16.top"),sQuery(id+"F11.wireOp",EDGE,"E16.left")])]})});
            var Q22;
            Q22=makeQuery(id+"F12.boolean.opBoolean","COPY",EDGE,{"derivedFrom":makeQuery(id+"F12.opExtrude","CAP_EDGE",EDGE,{"disambiguationData":[OSD([sQuery(id+"F11.wireOp",EDGE,"E16.left")])],"isStart":false})});
            var Q23;
            {var subQ0=sQuery(id+"F3.wireOp",EDGE,"E1.left");var subQ1=sQuery(id+"F3.wireOp",EDGE,"E1.top");Q23=makeQuery(id+"F12.boolean.opBoolean","SPLIT",EDGE,{"disambiguationData":[TD([makeQuery(id+"F4.opExtrude","SWEPT_FACE",FACE,{"disambiguationData":[OSD([subQ0])]})])],"derivedFrom":makeQuery(id+"F4.opExtrude","CAP_EDGE",EDGE,{"disambiguationData":[OSD([subQ1])],"isStart":false})});}
            var Q24;
            {var subQ0=sQuery(id+"F3.wireOp",EDGE,"E2.1");var subQ1=sQuery(id+"F3.wireOp",EDGE,"E2.0");Q24=makeQuery(id+"F12.boolean.opBoolean","SPLIT",EDGE,{"disambiguationData":[TD([makeQuery(id+"F4.opExtrude","SWEPT_FACE",FACE,{"disambiguationData":[OSD([subQ0])]})])],"derivedFrom":makeQuery(id+"F4.opExtrude","CAP_EDGE",EDGE,{"disambiguationData":[OSD([subQ1])],"isStart":false})});}
            var Q25;
            Q25=makeQuery(id+"F17.boolean.opBoolean","COPY",EDGE,{"derivedFrom":makeQuery(id+"F17.opExtrude","CAP_EDGE",EDGE,{"disambiguationData":[OSD([sQuery(id+"F16.wireOp",EDGE,"E22.0.8.0")])],"isStart":false})});
            var Q26;
            Q26=makeQuery(id+"F17.boolean.opBoolean","COPY",EDGE,{"derivedFrom":makeQuery(id+"F17.opExtrude","CAP_EDGE",EDGE,{"disambiguationData":[OSD([sQuery(id+"F16.wireOp",EDGE,"E21.0.7.0")])],"isStart":false})});
            var Q27;
            Q27=makeQuery(id+"F17.boolean.opBoolean","COPY",EDGE,{"derivedFrom":makeQuery(id+"F17.opExtrude","CAP_EDGE",EDGE,{"disambiguationData":[OSD([sQuery(id+"F16.wireOp",EDGE,"E21.0.6.0")])],"isStart":false})});
            var Q28;
            Q28=makeQuery(id+"F17.boolean.opBoolean","COPY",EDGE,{"derivedFrom":makeQuery(id+"F17.opExtrude","CAP_EDGE",EDGE,{"disambiguationData":[OSD([sQuery(id+"F16.wireOp",EDGE,"E20.5.0.0")])],"isStart":false})});
            var Q29;
            Q29=makeQuery(id+"F17.boolean.opBoolean","COPY",EDGE,{"derivedFrom":makeQuery(id+"F17.opExtrude","CAP_EDGE",EDGE,{"disambiguationData":[OSD([sQuery(id+"F16.wireOp",EDGE,"E20.4.0.0")])],"isStart":false})});
            var Q30;
            Q30=makeQuery(id+"F17.boolean.opBoolean","COPY",EDGE,{"derivedFrom":makeQuery(id+"F17.opExtrude","CAP_EDGE",EDGE,{"disambiguationData":[OSD([sQuery(id+"F16.wireOp",EDGE,"E20.3.0.0")])],"isStart":false})});
            var Q31;
            Q31=makeQuery(id+"F17.boolean.opBoolean","COPY",EDGE,{"derivedFrom":makeQuery(id+"F17.opExtrude","CAP_EDGE",EDGE,{"disambiguationData":[OSD([sQuery(id+"F16.wireOp",EDGE,"E20.2.0.0")])],"isStart":false})});
            var Q32;
            Q32=makeQuery(id+"F17.boolean.opBoolean","COPY",EDGE,{"derivedFrom":makeQuery(id+"F17.opExtrude","CAP_EDGE",EDGE,{"disambiguationData":[OSD([sQuery(id+"F16.wireOp",EDGE,"E20.1.0.0")])],"isStart":false})});
            var Q33;
            Q33=makeQuery(id+"F17.boolean.opBoolean","COPY",EDGE,{"derivedFrom":makeQuery(id+"F17.opExtrude","CAP_EDGE",EDGE,{"disambiguationData":[OSD([sQuery(id+"F16.wireOp",EDGE,"E19")])],"isStart":false})});
            var Q34;
            Q34=makeQuery(id+"F12.boolean.opBoolean","COPY",EDGE,{"derivedFrom":makeQuery(id+"F12.opExtrude","CAP_EDGE",EDGE,{"disambiguationData":[OSD([sQuery(id+"F11.wireOp",EDGE,"E15.top")])],"isStart":false})});
            var Q35;
            Q35=makeQuery(id+"F12.boolean.opBoolean","COPY",EDGE,{"derivedFrom":makeQuery(id+"F12.opExtrude","CAP_EDGE",EDGE,{"disambiguationData":[OSD([sQuery(id+"F11.wireOp",EDGE,"E15.top")])],"isStart":true})});
            var Q36;
            Q36=makeQuery(id+"F12.boolean.opBoolean","COPY",EDGE,{"derivedFrom":makeQuery(id+"F12.opExtrude","SWEPT_EDGE",EDGE,{"disambiguationData":[OSD([sQuery(id+"F3.wireOp",EDGE,"E2.3"),sQuery(id+"F11.wireOp",EDGE,"E15.top"),sQuery(id+"F11.wireOp",EDGE,"E15.left")])]})});
            var Q37;
            Q37=makeQuery(id+"F12.boolean.opBoolean","COPY",EDGE,{"derivedFrom":makeQuery(id+"F12.opExtrude","SWEPT_EDGE",EDGE,{"disambiguationData":[OSD([sQuery(id+"F3.wireOp",EDGE,"E1.right"),sQuery(id+"F11.wireOp",EDGE,"E15.top"),sQuery(id+"F11.wireOp",EDGE,"E15.right")])]})});
            var Q38;
            Q38=makeQuery(id+"F12.boolean.opBoolean","COPY",EDGE,{"derivedFrom":makeQuery(id+"F12.opExtrude","CAP_EDGE",EDGE,{"disambiguationData":[OSD([sQuery(id+"F11.wireOp",EDGE,"E15.bottom")])],"isStart":false})});
            var Q39;
            Q39=makeQuery(id+"F19.boolean.opBoolean","MERGE",EDGE,{"derivedFrom":[makeQuery(id+"F12.boolean.opBoolean","COPY",EDGE,{"derivedFrom":makeQuery(id+"F12.opExtrude","SWEPT_EDGE",EDGE,{"disambiguationData":[OSD([sQuery(id+"F3.wireOp",EDGE,"E2.3"),sQuery(id+"F11.wireOp",EDGE,"E15.bottom"),sQuery(id+"F11.wireOp",EDGE,"E15.left")])]})}),makeQuery(id+"F19.opExtrude","SWEPT_EDGE",EDGE,{"disambiguationData":[OSD([sQuery(id+"F18.wireOp",EDGE,"E23.bottom"),sQuery(id+"F18.wireOp",EDGE,"E25")])]})]});
            var Q40;
            Q40=makeQuery(id+"F19.opExtrude","CAP_EDGE",EDGE,{"disambiguationData":[OSD([sQuery(id+"F18.wireOp",EDGE,"E23.bottom")])],"isStart":false});
            var Q41;
            Q41=makeQuery(id+"F19.boolean.opBoolean","MERGE",EDGE,{"derivedFrom":[makeQuery(id+"F12.boolean.opBoolean","COPY",EDGE,{"derivedFrom":makeQuery(id+"F12.opExtrude","SWEPT_EDGE",EDGE,{"disambiguationData":[OSD([sQuery(id+"F3.wireOp",EDGE,"E1.right"),sQuery(id+"F11.wireOp",EDGE,"E15.bottom"),sQuery(id+"F11.wireOp",EDGE,"E15.right")])]})}),makeQuery(id+"F19.opExtrude","SWEPT_EDGE",EDGE,{"disambiguationData":[OSD([sQuery(id+"F18.wireOp",EDGE,"E23.bottom"),sQuery(id+"F18.wireOp",EDGE,"E23.left")])]})]});
            var Q42;
            Q42=makeQuery(id+"F19.opExtrude","CAP_EDGE",EDGE,{"disambiguationData":[OSD([sQuery(id+"F18.wireOp",EDGE,"E23.left")])],"isStart":false});
            var Q43;
            Q43=makeQuery(id+"F19.boolean.opBoolean","MERGE",EDGE,{"derivedFrom":[makeQuery(id+"F12.boolean.opBoolean","COPY",EDGE,{"derivedFrom":makeQuery(id+"F12.opExtrude","SWEPT_EDGE",EDGE,{"disambiguationData":[OSD([sQuery(id+"F3.wireOp",EDGE,"E1.right"),sQuery(id+"F11.wireOp",EDGE,"E15.bottom"),sQuery(id+"F11.wireOp",EDGE,"E15.right")])]})}),makeQuery(id+"F19.opExtrude","SWEPT_EDGE",EDGE,{"disambiguationData":[OSD([sQuery(id+"F18.wireOp",EDGE,"E23.bottom"),sQuery(id+"F18.wireOp",EDGE,"E23.left")])]})]});
            var Q44;
            Q44=makeQuery(id+"F12.boolean.opBoolean","COPY",EDGE,{"derivedFrom":makeQuery(id+"F12.opExtrude","CAP_EDGE",EDGE,{"disambiguationData":[OSD([sQuery(id+"F11.wireOp",EDGE,"E18.left")])],"isStart":true})});
            var Q45;
            Q45=makeQuery(id+"F12.boolean.opBoolean","COPY",EDGE,{"derivedFrom":makeQuery(id+"F12.opExtrude","SWEPT_EDGE",EDGE,{"disambiguationData":[OSD([sQuery(id+"F3.wireOp",EDGE,"E2.2"),sQuery(id+"F11.wireOp",EDGE,"E18.top"),sQuery(id+"F11.wireOp",EDGE,"E18.left")])]})});
            var Q46;
            Q46=makeQuery(id+"F12.boolean.opBoolean","COPY",EDGE,{"derivedFrom":makeQuery(id+"F12.opExtrude","SWEPT_EDGE",EDGE,{"disambiguationData":[OSD([sQuery(id+"F3.wireOp",EDGE,"E1.bottom"),sQuery(id+"F11.wireOp",EDGE,"E18.bottom"),sQuery(id+"F11.wireOp",EDGE,"E18.left")])]})});
            var Q47;
            Q47=makeQuery(id+"F12.boolean.opBoolean","COPY",EDGE,{"derivedFrom":makeQuery(id+"F12.opExtrude","CAP_EDGE",EDGE,{"disambiguationData":[OSD([sQuery(id+"F11.wireOp",EDGE,"E18.left")])],"isStart":false})});
            var Q48;
            Q48=makeQuery(id+"F12.boolean.opBoolean","COPY",EDGE,{"derivedFrom":makeQuery(id+"F12.opExtrude","SWEPT_EDGE",EDGE,{"disambiguationData":[OSD([sQuery(id+"F3.wireOp",EDGE,"E2.2"),sQuery(id+"F11.wireOp",EDGE,"E18.top"),sQuery(id+"F11.wireOp",EDGE,"E18.right")])]})});
            var Q49;
            Q49=makeQuery(id+"F12.boolean.opBoolean","COPY",EDGE,{"derivedFrom":makeQuery(id+"F12.opExtrude","CAP_EDGE",EDGE,{"disambiguationData":[OSD([sQuery(id+"F11.wireOp",EDGE,"E18.right")])],"isStart":true})});
            var Q50;
            Q50=makeQuery(id+"F12.boolean.opBoolean","COPY",EDGE,{"derivedFrom":makeQuery(id+"F12.opExtrude","SWEPT_EDGE",EDGE,{"disambiguationData":[OSD([sQuery(id+"F3.wireOp",EDGE,"E1.bottom"),sQuery(id+"F11.wireOp",EDGE,"E18.bottom"),sQuery(id+"F11.wireOp",EDGE,"E18.right")])]})});
            var Q51;
            Q51=makeQuery(id+"F12.boolean.opBoolean","COPY",EDGE,{"derivedFrom":makeQuery(id+"F12.opExtrude","CAP_EDGE",EDGE,{"disambiguationData":[OSD([sQuery(id+"F11.wireOp",EDGE,"E18.right")])],"isStart":false})});
            var Q52;
            {var subQ0=sQuery(id+"F3.wireOp",EDGE,"E1.bottom");Q52=makeQuery(id+"F12.boolean.opBoolean","SPLIT",EDGE,{"disambiguationData":[TD([makeQuery(id+"F4.opExtrude","SWEPT_FACE",FACE,{"disambiguationData":[OSD([sQuery(id+"F3.wireOp",EDGE,"E1.left")])]})])],"derivedFrom":makeQuery(id+"F4.opExtrude","CAP_EDGE",EDGE,{"disambiguationData":[OSD([subQ0])],"isStart":true})});}
            var Q53;
            {var subQ0=sQuery(id+"F3.wireOp",EDGE,"E1.bottom");var subQ1=sQuery(id+"F3.wireOp",EDGE,"E1.left");Q53=makeQuery(id+"F12.boolean.opBoolean","SPLIT",EDGE,{"disambiguationData":[TD([makeQuery(id+"F4.opExtrude","SWEPT_FACE",FACE,{"disambiguationData":[OSD([subQ1])]})])],"derivedFrom":makeQuery(id+"F4.opExtrude","CAP_EDGE",EDGE,{"disambiguationData":[OSD([subQ0])],"isStart":false})});}
            var Q54;
            {var subQ0=sQuery(id+"F3.wireOp",EDGE,"E2.2");var subQ1=sQuery(id+"F3.wireOp",EDGE,"E2.1");Q54=makeQuery(id+"F12.boolean.opBoolean","SPLIT",EDGE,{"disambiguationData":[TD([makeQuery(id+"F4.opExtrude","SWEPT_FACE",FACE,{"disambiguationData":[OSD([subQ1])]})])],"derivedFrom":makeQuery(id+"F4.opExtrude","CAP_EDGE",EDGE,{"disambiguationData":[OSD([subQ0])],"isStart":false})});}
            var Q55;
            Q55=makeQuery(id+"F12.boolean.opBoolean","COPY",EDGE,{"derivedFrom":makeQuery(id+"F12.opExtrude","CAP_EDGE",EDGE,{"disambiguationData":[OSD([sQuery(id+"F11.wireOp",EDGE,"E17.bottom")])],"isStart":true})});
            var Q56;
            Q56=makeQuery(id+"F12.boolean.opBoolean","COPY",EDGE,{"derivedFrom":makeQuery(id+"F12.opExtrude","SWEPT_EDGE",EDGE,{"disambiguationData":[OSD([sQuery(id+"F3.wireOp",EDGE,"E2.1"),sQuery(id+"F11.wireOp",EDGE,"E17.bottom"),sQuery(id+"F11.wireOp",EDGE,"E17.left")])]})});
            var Q57;
            Q57=makeQuery(id+"F12.boolean.opBoolean","COPY",EDGE,{"derivedFrom":makeQuery(id+"F12.opExtrude","SWEPT_EDGE",EDGE,{"disambiguationData":[OSD([sQuery(id+"F3.wireOp",EDGE,"E1.left"),sQuery(id+"F11.wireOp",EDGE,"E17.bottom"),sQuery(id+"F11.wireOp",EDGE,"E17.right")])]})});
            var Q58;
            Q58=makeQuery(id+"F12.boolean.opBoolean","COPY",EDGE,{"derivedFrom":makeQuery(id+"F12.opExtrude","CAP_EDGE",EDGE,{"disambiguationData":[OSD([sQuery(id+"F11.wireOp",EDGE,"E17.bottom")])],"isStart":false})});
            var Q59;
            Q59=makeQuery(id+"F12.boolean.opBoolean","COPY",EDGE,{"derivedFrom":makeQuery(id+"F12.opExtrude","CAP_EDGE",EDGE,{"disambiguationData":[OSD([sQuery(id+"F11.wireOp",EDGE,"E17.top")])],"isStart":false})});
            var Q60;
            Q60=makeQuery(id+"F19.opExtrude","CAP_EDGE",EDGE,{"disambiguationData":[OSD([sQuery(id+"F18.wireOp",EDGE,"E24.top")])],"isStart":false});
            var Q61;
            Q61=makeQuery(id+"F19.boolean.opBoolean","MERGE",EDGE,{"derivedFrom":[makeQuery(id+"F12.boolean.opBoolean","COPY",EDGE,{"derivedFrom":makeQuery(id+"F12.opExtrude","SWEPT_EDGE",EDGE,{"disambiguationData":[OSD([sQuery(id+"F3.wireOp",EDGE,"E1.left"),sQuery(id+"F11.wireOp",EDGE,"E17.top"),sQuery(id+"F11.wireOp",EDGE,"E17.right")])]})}),makeQuery(id+"F19.opExtrude","SWEPT_EDGE",EDGE,{"disambiguationData":[OSD([sQuery(id+"F18.wireOp",EDGE,"E24.top"),sQuery(id+"F18.wireOp",EDGE,"E24.right")])]})]});
            var Q62;
            Q62=makeQuery(id+"F19.boolean.opBoolean","MERGE",EDGE,{"derivedFrom":[makeQuery(id+"F12.boolean.opBoolean","COPY",EDGE,{"derivedFrom":makeQuery(id+"F12.opExtrude","SWEPT_EDGE",EDGE,{"disambiguationData":[OSD([sQuery(id+"F3.wireOp",EDGE,"E1.left"),sQuery(id+"F11.wireOp",EDGE,"E17.top"),sQuery(id+"F11.wireOp",EDGE,"E17.right")])]})}),makeQuery(id+"F19.opExtrude","SWEPT_EDGE",EDGE,{"disambiguationData":[OSD([sQuery(id+"F18.wireOp",EDGE,"E24.top"),sQuery(id+"F18.wireOp",EDGE,"E24.right")])]})]});
            var Q63;
            Q63=makeQuery(id+"F19.opExtrude","CAP_EDGE",EDGE,{"disambiguationData":[OSD([sQuery(id+"F18.wireOp",EDGE,"E24.right")])],"isStart":false});
            var Q64;
            Q64=makeQuery(id+"F19.opExtrude","CAP_EDGE",EDGE,{"disambiguationData":[OSD([sQuery(id+"F18.wireOp",EDGE,"E24.left"),sQuery(id+"F18.wireOp",EDGE,"DAfPsO16-irwq-zqkO-su3k-pfqR2VeTVtR9")])],"isStart":false});
            var Q65;
            Q65=makeQuery(id+"F19.boolean.opBoolean","MERGE",EDGE,{"derivedFrom":[makeQuery(id+"F12.boolean.opBoolean","COPY",EDGE,{"derivedFrom":makeQuery(id+"F12.opExtrude","SWEPT_EDGE",EDGE,{"disambiguationData":[OSD([sQuery(id+"F3.wireOp",EDGE,"E1.left"),sQuery(id+"F11.wireOp",EDGE,"E17.top"),sQuery(id+"F11.wireOp",EDGE,"E17.right")])]})}),makeQuery(id+"F19.opExtrude","SWEPT_EDGE",EDGE,{"disambiguationData":[OSD([sQuery(id+"F18.wireOp",EDGE,"E24.top"),sQuery(id+"F18.wireOp",EDGE,"E24.right")])]})]});
            var Q66;
            {var subQ0=sQuery(id+"F3.wireOp",EDGE,"E2.1");var subQ1=sQuery(id+"F3.wireOp",EDGE,"E2.0");var subQ2=sQuery(id+"F3.wireOp",EDGE,"E1.left");var subQ3=sQuery(id+"F3.wireOp",EDGE,"E1.top");Q66=makeQuery(id+"F14.opFillet","BLEND_EDGE",EDGE,{"blendedFrom":[makeQuery(id+"F4.opExtrude","SWEPT_EDGE",EDGE,{"disambiguationData":[OSD([subQ1,subQ0])]}),makeQuery(id+"F12.boolean.opBoolean","SPLIT",FACE,{"disambiguationData":[TD([makeQuery(id+"F12.opExtrude","SWEPT_FACE",FACE,{"disambiguationData":[OSD([sQuery(id+"F11.wireOp",EDGE,"E16.left")])]})])],"derivedFrom":makeQuery(id+"F4.opExtrude","CAP_FACE",FACE,{"disambiguationData":[OSD([sQuery(id+"F3.wireOp",EDGE,"E1.bottom"),subQ3,subQ2,sQuery(id+"F3.wireOp",EDGE,"E1.right"),subQ1,subQ0,sQuery(id+"F3.wireOp",EDGE,"E2.2"),sQuery(id+"F3.wireOp",EDGE,"E2.3")])],"isStart":false})})],"blendedInto":[makeQuery(id+"F12.boolean.opBoolean","SPLIT",FACE,{"disambiguationData":[TD([makeQuery(id+"F12.opExtrude","SWEPT_FACE",FACE,{"disambiguationData":[OSD([sQuery(id+"F11.wireOp",EDGE,"E16.left")])]})])],"derivedFrom":makeQuery(id+"F4.opExtrude","CAP_FACE",FACE,{"disambiguationData":[OSD([sQuery(id+"F3.wireOp",EDGE,"E1.bottom"),subQ3,subQ2,sQuery(id+"F3.wireOp",EDGE,"E1.right"),subQ1,subQ0,sQuery(id+"F3.wireOp",EDGE,"E2.2"),sQuery(id+"F3.wireOp",EDGE,"E2.3")])],"isStart":false})})]});}
            var Q67;
            {var subQ0=sQuery(id+"F3.wireOp",EDGE,"E2.3");var subQ1=sQuery(id+"F3.wireOp",EDGE,"E2.2");var subQ2=sQuery(id+"F3.wireOp",EDGE,"E1.right");var subQ3=sQuery(id+"F3.wireOp",EDGE,"E1.bottom");Q67=makeQuery(id+"F14.opFillet","BLEND_EDGE",EDGE,{"blendedFrom":[makeQuery(id+"F4.opExtrude","SWEPT_EDGE",EDGE,{"disambiguationData":[OSD([subQ1,subQ0])]}),makeQuery(id+"F12.boolean.opBoolean","SPLIT",FACE,{"disambiguationData":[TD([makeQuery(id+"F12.opExtrude","SWEPT_FACE",FACE,{"disambiguationData":[OSD([sQuery(id+"F11.wireOp",EDGE,"E15.bottom")])]})])],"derivedFrom":makeQuery(id+"F4.opExtrude","CAP_FACE",FACE,{"disambiguationData":[OSD([subQ3,sQuery(id+"F3.wireOp",EDGE,"E1.top"),sQuery(id+"F3.wireOp",EDGE,"E1.left"),subQ2,sQuery(id+"F3.wireOp",EDGE,"E2.0"),sQuery(id+"F3.wireOp",EDGE,"E2.1"),subQ1,subQ0])],"isStart":false})})],"blendedInto":[makeQuery(id+"F12.boolean.opBoolean","SPLIT",FACE,{"disambiguationData":[TD([makeQuery(id+"F12.opExtrude","SWEPT_FACE",FACE,{"disambiguationData":[OSD([sQuery(id+"F11.wireOp",EDGE,"E15.bottom")])]})])],"derivedFrom":makeQuery(id+"F4.opExtrude","CAP_FACE",FACE,{"disambiguationData":[OSD([subQ3,sQuery(id+"F3.wireOp",EDGE,"E1.top"),sQuery(id+"F3.wireOp",EDGE,"E1.left"),subQ2,sQuery(id+"F3.wireOp",EDGE,"E2.0"),sQuery(id+"F3.wireOp",EDGE,"E2.1"),subQ1,subQ0])],"isStart":false})})]});}
            var Q68;
            {var subQ0=sQuery(id+"F3.wireOp",EDGE,"E1.bottom");var subQ1=sQuery(id+"F3.wireOp",EDGE,"E1.right");Q68=makeQuery(id+"F12.boolean.opBoolean","SPLIT",EDGE,{"disambiguationData":[TD([makeQuery(id+"F4.opExtrude","SWEPT_FACE",FACE,{"disambiguationData":[OSD([subQ1])]})])],"derivedFrom":makeQuery(id+"F4.opExtrude","CAP_EDGE",EDGE,{"disambiguationData":[OSD([subQ0])],"isStart":false})});}
            var Q69;
            Q69=makeQuery(id+"F19.opExtrude","CAP_EDGE",EDGE,{"disambiguationData":[OSD([sQuery(id+"F18.wireOp",EDGE,"1EWOjgto-lhHO-r0mv-XYk0-ZaQik07Pemkt")])],"isStart":false});
            fillet(context, id + "F20", {"entities" : qUnion([Q0, Q1, Q2, Q3, Q4, Q5, Q6, Q7, Q8, Q9, Q10, Q11, Q12, Q13, Q14, Q15, Q16, Q17, Q18, Q19, Q20, Q21, Q22, Q23, Q24, Q25, Q26, Q27, Q28, Q29, Q30, Q31, Q32, Q33, Q34, Q35, Q36, Q37, Q38, Q39, Q40, Q41, Q42, Q43, Q44, Q45, Q46, Q47, Q48, Q49, Q50, Q51, Q52, Q53, Q54, Q55, Q56, Q57, Q58, Q59, Q60, Q61, Q62, Q63, Q64, Q65, Q66, Q67, Q68, Q69]), "radius" : 1.27 * mm, "tangentPropagation" : true, "allowEdgeOverflow" : false});
        }
        {
            var Q0;
            Q0=makeQuery(id+"F1.opExtrude","CAP_EDGE",EDGE,{"disambiguationData":[OSD([sQuery(id+"F0.wireOp",EDGE,"E0.top")])],"isStart":false});
            var Q1;
            {var subQ0=sQuery(id+"F0.wireOp",EDGE,"E0.top");Q1=makeQuery(id+"F2.opShell","OFFSET_EDGE",EDGE,{"disambiguationData":[OSD([subQ0]),TDD([makeQuery(id+"F1.opExtrude","CAP_EDGE",EDGE,{"disambiguationData":[OSD([subQ0])],"isStart":false})])]});}
            var Q2;
            Q2=makeQuery(id+"F8.boolean.opBoolean","COPY",EDGE,{"derivedFrom":makeQuery(id+"F8.opExtrude","SWEPT_EDGE",EDGE,{"disambiguationData":[OSD([sQuery(id+"F0.wireOp",EDGE,"E0.bottom"),sQuery(id+"F7.wireOp",EDGE,"E8"),sQuery(id+"F7.wireOp",EDGE,"E9")])]})});
            var Q3;
            Q3=makeQuery(id+"F8.boolean.opBoolean","INTERSECT",EDGE,{"derivedFrom":[makeQuery(id+"F1.opExtrude","SWEPT_FACE",FACE,{"disambiguationData":[OSD([sQuery(id+"F0.wireOp",EDGE,"E0.top")])]}),makeQuery(id+"F8.opExtrude","SWEPT_FACE",FACE,{"disambiguationData":[OSD([sQuery(id+"F7.wireOp",EDGE,"E10")])]})]});
            var Q4;
            Q4=makeQuery(id+"F8.boolean.opBoolean","COPY",EDGE,{"derivedFrom":makeQuery(id+"F8.opExtrude","SWEPT_EDGE",EDGE,{"disambiguationData":[OSD([sQuery(id+"F0.wireOp",EDGE,"E0.bottom"),sQuery(id+"F7.wireOp",EDGE,"E7"),sQuery(id+"F7.wireOp",EDGE,"E8")])]})});
            var Q5;
            Q5=makeQuery(id+"F8.boolean.opBoolean","INTERSECT",EDGE,{"derivedFrom":[makeQuery(id+"F2.opShell","OFFSET_FACE",FACE,{"disambiguationData":[OSD([sQuery(id+"F0.wireOp",EDGE,"E0.top")])]}),makeQuery(id+"F8.opExtrude","SWEPT_FACE",FACE,{"disambiguationData":[OSD([sQuery(id+"F7.wireOp",EDGE,"E10")])]})]});
            var Q6;
            Q6=makeQuery(id+"F8.boolean.opBoolean","INTERSECT",EDGE,{"derivedFrom":[makeQuery(id+"F2.opShell","OFFSET_FACE",FACE,{"disambiguationData":[OSD([sQuery(id+"F0.wireOp",EDGE,"E0.bottom")])]}),makeQuery(id+"F8.opExtrude","SWEPT_FACE",FACE,{"disambiguationData":[OSD([sQuery(id+"F7.wireOp",EDGE,"E7")])]})]});
            var Q7;
            Q7=makeQuery(id+"F8.boolean.opBoolean","COPY",EDGE,{"derivedFrom":makeQuery(id+"F8.opExtrude","SWEPT_EDGE",EDGE,{"disambiguationData":[OSD([sQuery(id+"F0.wireOp",EDGE,"E0.bottom"),sQuery(id+"F7.wireOp",EDGE,"E7"),sQuery(id+"F7.wireOp",EDGE,"E8")])]})});
            var Q8;
            {var subQ0=sQuery(id+"F0.wireOp",EDGE,"E0.left");var subQ1=sQuery(id+"F0.wireOp",EDGE,"E0.bottom");Q8=makeQuery(id+"F8.boolean.opBoolean","SPLIT",EDGE,{"disambiguationData":[TD([makeQuery(id+"F2.opShell","OFFSET_FACE",FACE,{"disambiguationData":[OSD([subQ0])]})])],"derivedFrom":makeQuery(id+"F2.opShell","OFFSET_EDGE",EDGE,{"disambiguationData":[OSD([subQ1]),TDD([makeQuery(id+"F1.opExtrude","CAP_EDGE",EDGE,{"disambiguationData":[OSD([subQ1])],"isStart":false})])]})});}
            var Q9;
            {var subQ0=sQuery(id+"F0.wireOp",EDGE,"E0.bottom");var subQ1=sQuery(id+"F0.wireOp",EDGE,"E0.left");Q9=makeQuery(id+"F8.boolean.opBoolean","SPLIT",EDGE,{"disambiguationData":[TD([makeQuery(id+"F1.opExtrude","SWEPT_FACE",FACE,{"disambiguationData":[OSD([subQ1])]})])],"derivedFrom":makeQuery(id+"F1.opExtrude","CAP_EDGE",EDGE,{"disambiguationData":[OSD([subQ0])],"isStart":false})});}
            var Q10;
            Q10=makeQuery(id+"F1.opExtrude","CAP_EDGE",EDGE,{"disambiguationData":[OSD([sQuery(id+"F0.wireOp",EDGE,"E0.top")])],"isStart":false});
            var Q11;
            {var subQ0=sQuery(id+"F0.wireOp",EDGE,"E0.top");Q11=makeQuery(id+"F2.opShell","OFFSET_EDGE",EDGE,{"disambiguationData":[OSD([subQ0]),TDD([makeQuery(id+"F1.opExtrude","CAP_EDGE",EDGE,{"disambiguationData":[OSD([subQ0])],"isStart":false})])]});}
            var Q12;
            Q12=makeQuery(id+"F8.boolean.opBoolean","COPY",EDGE,{"derivedFrom":makeQuery(id+"F8.opExtrude","CAP_EDGE",EDGE,{"disambiguationData":[OSD([sQuery(id+"F7.wireOp",EDGE,"E10")])],"isStart":true})});
            var Q13;
            Q13=makeQuery(id+"F8.boolean.opBoolean","COPY",EDGE,{"derivedFrom":makeQuery(id+"F8.opExtrude","SWEPT_EDGE",EDGE,{"disambiguationData":[OSD([sQuery(id+"F0.wireOp",EDGE,"E0.bottom"),sQuery(id+"F7.wireOp",EDGE,"E8"),sQuery(id+"F7.wireOp",EDGE,"E9")])]})});
            var Q14;
            {var subQ0=sQuery(id+"F0.wireOp",EDGE,"E0.bottom");var subQ1=sQuery(id+"F0.wireOp",EDGE,"E0.right");Q14=makeQuery(id+"F8.boolean.opBoolean","SPLIT",EDGE,{"disambiguationData":[TD([makeQuery(id+"F1.opExtrude","SWEPT_FACE",FACE,{"disambiguationData":[OSD([subQ1])]})])],"derivedFrom":makeQuery(id+"F1.opExtrude","CAP_EDGE",EDGE,{"disambiguationData":[OSD([subQ0])],"isStart":false})});}
            var Q15;
            {var subQ0=sQuery(id+"F0.wireOp",EDGE,"E0.right");var subQ1=sQuery(id+"F0.wireOp",EDGE,"E0.bottom");Q15=makeQuery(id+"F8.boolean.opBoolean","SPLIT",EDGE,{"disambiguationData":[TD([makeQuery(id+"F2.opShell","OFFSET_FACE",FACE,{"disambiguationData":[OSD([subQ0])]})])],"derivedFrom":makeQuery(id+"F2.opShell","OFFSET_EDGE",EDGE,{"disambiguationData":[OSD([subQ1]),TDD([makeQuery(id+"F1.opExtrude","CAP_EDGE",EDGE,{"disambiguationData":[OSD([subQ1])],"isStart":false})])]})});}
            var Q16;
            Q16=makeQuery(id+"F10.boolean.opBoolean","COPY",EDGE,{"derivedFrom":makeQuery(id+"F10.opExtrude","CAP_EDGE",EDGE,{"disambiguationData":[OSD([sQuery(id+"F9.wireOp",EDGE,"E13")])],"isStart":true})});
            var Q17;
            Q17=makeQuery(id+"F10.boolean.opBoolean","INTERSECT",EDGE,{"derivedFrom":[makeQuery(id+"F2.opShell","OFFSET_FACE",FACE,{"disambiguationData":[OSD([sQuery(id+"F0.wireOp",EDGE,"E0.right")])]}),makeQuery(id+"F10.opExtrude","SWEPT_FACE",FACE,{"disambiguationData":[OSD([sQuery(id+"F9.wireOp",EDGE,"E11")])]})]});
            var Q18;
            Q18=makeQuery(id+"F10.boolean.opBoolean","COPY",EDGE,{"derivedFrom":makeQuery(id+"F10.opExtrude","SWEPT_EDGE",EDGE,{"disambiguationData":[OSD([sQuery(id+"F0.wireOp",EDGE,"E0.right"),sQuery(id+"F9.wireOp",EDGE,"E11"),sQuery(id+"F9.wireOp",EDGE,"E12")])]})});
            var Q19;
            Q19=makeQuery(id+"F10.boolean.opBoolean","COPY",EDGE,{"derivedFrom":makeQuery(id+"F10.opExtrude","SWEPT_EDGE",EDGE,{"disambiguationData":[OSD([sQuery(id+"F0.wireOp",EDGE,"E0.right"),sQuery(id+"F9.wireOp",EDGE,"E12"),sQuery(id+"F9.wireOp",EDGE,"E13")])]})});
            var Q20;
            Q20=makeQuery(id+"F10.boolean.opBoolean","INTERSECT",EDGE,{"derivedFrom":[makeQuery(id+"F2.opShell","OFFSET_FACE",FACE,{"disambiguationData":[OSD([sQuery(id+"F0.wireOp",EDGE,"E0.left")])]}),makeQuery(id+"F10.opExtrude","SWEPT_FACE",FACE,{"disambiguationData":[OSD([sQuery(id+"F9.wireOp",EDGE,"E14")])]})]});
            var Q21;
            Q21=makeQuery(id+"F10.boolean.opBoolean","INTERSECT",EDGE,{"derivedFrom":[makeQuery(id+"F1.opExtrude","SWEPT_FACE",FACE,{"disambiguationData":[OSD([sQuery(id+"F0.wireOp",EDGE,"E0.left")])]}),makeQuery(id+"F10.opExtrude","SWEPT_FACE",FACE,{"disambiguationData":[OSD([sQuery(id+"F9.wireOp",EDGE,"E11")])]})]});
            var Q22;
            Q22=makeQuery(id+"F10.boolean.opBoolean","COPY",EDGE,{"derivedFrom":makeQuery(id+"F10.opExtrude","SWEPT_EDGE",EDGE,{"disambiguationData":[OSD([sQuery(id+"F0.wireOp",EDGE,"E0.right"),sQuery(id+"F9.wireOp",EDGE,"E11"),sQuery(id+"F9.wireOp",EDGE,"E12")])]})});
            var Q23;
            Q23=makeQuery(id+"F10.boolean.opBoolean","COPY",EDGE,{"derivedFrom":makeQuery(id+"F10.opExtrude","SWEPT_EDGE",EDGE,{"disambiguationData":[OSD([sQuery(id+"F0.wireOp",EDGE,"E0.right"),sQuery(id+"F9.wireOp",EDGE,"E12"),sQuery(id+"F9.wireOp",EDGE,"E13")])]})});
            var Q24;
            Q24=makeQuery(id+"FnIjyfwqoN67EGb_2.boolean.opBoolean","INTERSECT",EDGE,{"derivedFrom":[makeQuery(id+"F2.opShell","OFFSET_FACE",FACE,{"disambiguationData":[OSD([sQuery(id+"F0.wireOp",EDGE,"E0.left")])]}),makeQuery(id+"FnIjyfwqoN67EGb_2.opExtrude","SWEPT_FACE",FACE,{"disambiguationData":[OSD([sQuery(id+"FAHIqezCOhTjNG8_2.wireOp",EDGE,"q8DLlluq-B3oI-w7Xp-zHWp-GYA7pbw8v9kt")])]})]});
            var Q25;
            Q25=makeQuery(id+"F5YvRMMHe4stEJj_2.boolean.opBoolean","INTERSECT",EDGE,{"derivedFrom":[makeQuery(id+"F2.opShell","OFFSET_FACE",FACE,{"disambiguationData":[OSD([sQuery(id+"F0.wireOp",EDGE,"E0.right")])]}),makeQuery(id+"F5YvRMMHe4stEJj_2.opExtrude","SWEPT_FACE",FACE,{"disambiguationData":[OSD([sQuery(id+"FnUOowWulHN1Gfi_2.wireOp",EDGE,"iOzeJWZC-AOQr-oXYK-y9gA-9Sb7wMRRJIBc")])]})]});
            var Q26;
            {var subQ0=sQuery(id+"F0.wireOp",EDGE,"E0.bottom");Q26=makeQuery(id+"F2.opShell","OFFSET_EDGE",EDGE,{"disambiguationData":[OSD([subQ0]),TDD([makeQuery(id+"F1.opExtrude","CAP_EDGE",EDGE,{"disambiguationData":[OSD([subQ0])],"isStart":true})])]});}
            fillet(context, id + "F21", {"entities" : qUnion([Q0, Q1, Q2, Q3, Q4, Q5, Q6, Q7, Q8, Q9, Q10, Q11, Q12, Q13, Q14, Q15, Q16, Q17, Q18, Q19, Q20, Q21, Q22, Q23, Q24, Q25, Q26]), "radius" : 1.27 * mm, "tangentPropagation" : true, "allowEdgeOverflow" : false});
        }
        {
            var Q0;
            Q0=makeQuery(id+"F1.opExtrude","SWEPT_FACE",FACE,{"disambiguationData":[OSD([sQuery(id+"F0.wireOp",EDGE,"E0.left")])]});
            var sketch = newSketch(context, id + "F22", { "sketchPlane" : qUnion([Q0])});
            skPoint(sketch, "E29", {"position": v(15.24, 18.41) * mm});
            skSolve(sketch);
        }
        {
            var Q0;
            Q0=sQuery(id+"F22.wireOp",VERTEX,"E29");
            var Q1;
            Q1=makeQuery(id+"F4.opExtrude","SWEPT_BODY",BODY,{"disambiguationData":[OSD([sQuery(id+"F3.wireOp",EDGE,"E1.bottom"),sQuery(id+"F3.wireOp",EDGE,"E1.top"),sQuery(id+"F3.wireOp",EDGE,"E1.left"),sQuery(id+"F3.wireOp",EDGE,"E1.right"),sQuery(id+"F3.wireOp",EDGE,"E2.0"),sQuery(id+"F3.wireOp",EDGE,"E2.1"),sQuery(id+"F3.wireOp",EDGE,"E2.2"),sQuery(id+"F3.wireOp",EDGE,"E2.3")])]});
            var Q2;
            Q2=makeQuery(id+"F1.opExtrude","SWEPT_BODY",BODY,{"disambiguationData":[OSD([sQuery(id+"F0.wireOp",EDGE,"E0.bottom"),sQuery(id+"F0.wireOp",EDGE,"E0.top"),sQuery(id+"F0.wireOp",EDGE,"E0.left"),sQuery(id+"F0.wireOp",EDGE,"E0.right")])]});
            hole(context, id + "F23", {"style" : HoleStyle.C_SINK, "endStyle" : HoleEndStyle.BLIND, "holeDiameter" : 2.95 * mm, "cSinkDiameter" : 5.38 * mm, "cSinkAngle" : 82 * degree, "holeDepth" : 12.7 * mm, "startFromSketch" : true, "locations" : qUnion([Q0]), "scope" : qUnion([Q1, Q2])});
        }
        {
            var Q0;
            Q0=makeQuery(id+"F1.opExtrude","SWEPT_FACE",FACE,{"disambiguationData":[OSD([sQuery(id+"F0.wireOp",EDGE,"E0.right")])]});
            var sketch = newSketch(context, id + "F24", { "sketchPlane" : qUnion([Q0])});
            skPoint(sketch, "E30", {"position": v(12.07, 18.41) * mm});
            skSolve(sketch);
        }
        {
            var Q0;
            Q0=sQuery(id+"F24.wireOp",VERTEX,"E30");
            var Q1;
            Q1=makeQuery(id+"F1.opExtrude","SWEPT_BODY",BODY,{"disambiguationData":[OSD([sQuery(id+"F0.wireOp",EDGE,"E0.bottom"),sQuery(id+"F0.wireOp",EDGE,"E0.top"),sQuery(id+"F0.wireOp",EDGE,"E0.left"),sQuery(id+"F0.wireOp",EDGE,"E0.right")])]});
            var Q2;
            Q2=makeQuery(id+"F4.opExtrude","SWEPT_BODY",BODY,{"disambiguationData":[OSD([sQuery(id+"F3.wireOp",EDGE,"E1.bottom"),sQuery(id+"F3.wireOp",EDGE,"E1.top"),sQuery(id+"F3.wireOp",EDGE,"E1.left"),sQuery(id+"F3.wireOp",EDGE,"E1.right"),sQuery(id+"F3.wireOp",EDGE,"E2.0"),sQuery(id+"F3.wireOp",EDGE,"E2.1"),sQuery(id+"F3.wireOp",EDGE,"E2.2"),sQuery(id+"F3.wireOp",EDGE,"E2.3")])]});
            hole(context, id + "F25", {"style" : HoleStyle.C_SINK, "endStyle" : HoleEndStyle.BLIND, "holeDiameter" : 2.95 * mm, "cSinkDiameter" : 5.38 * mm, "cSinkAngle" : 82 * degree, "holeDepth" : 12.7 * mm, "locations" : qUnion([Q0]), "scope" : qUnion([Q1, Q2])});
        }
        {
            var Q0;
            Q0=makeQuery(id+"F6.opExtrude","CAP_FACE",FACE,{"disambiguationData":[OSD([sQuery(id+"F5.wireOp",EDGE,"E3.0"),sQuery(id+"F5.wireOp",EDGE,"E4.0"),sQuery(id+"F5.wireOp",EDGE,"E5.0"),sQuery(id+"F5.wireOp",EDGE,"E6.0")])],"isStart":false});
            var sketch = newSketch(context, id + "F26", { "sketchPlane" : qUnion([Q0])});
            skLineSegment(sketch, "E31.bottom", {"start": v(69.85, 15.88) * mm, "end": v(73.02, 15.88) * mm});
            skLineSegment(sketch, "E31.top", {"start": v(69.85, -15.87) * mm, "end": v(73.03, -15.87) * mm});
            skLineSegment(sketch, "E31.left", {"start": v(69.85, 15.88) * mm, "end": v(69.85, -15.87) * mm});
            skLineSegment(sketch, "E31.right", {"start": v(73.02, 15.88) * mm, "end": v(73.03, -15.87) * mm});
            skLineSegment(sketch, "E32.bottom", {"start": v(57.15, 15.88) * mm, "end": v(53.97, 15.88) * mm});
            skLineSegment(sketch, "E32.top", {"start": v(57.15, -15.87) * mm, "end": v(53.98, -15.87) * mm});
            skLineSegment(sketch, "E32.left", {"start": v(57.15, 15.88) * mm, "end": v(57.15, -15.87) * mm});
            skLineSegment(sketch, "E32.right", {"start": v(53.97, 15.88) * mm, "end": v(53.98, -15.87) * mm});
            skLineSegment(sketch, "E33.bottom", {"start": v(41.27, 15.88) * mm, "end": v(38.1, 15.88) * mm});
            skLineSegment(sketch, "E33.top", {"start": v(41.28, -15.87) * mm, "end": v(38.1, -15.87) * mm});
            skLineSegment(sketch, "E33.left", {"start": v(41.27, 15.88) * mm, "end": v(41.28, -15.87) * mm});
            skLineSegment(sketch, "E33.right", {"start": v(38.1, 15.88) * mm, "end": v(38.1, -15.87) * mm});
            skLineSegment(sketch, "E34.bottom", {"start": v(25.4, 15.88) * mm, "end": v(22.23, 15.88) * mm});
            skLineSegment(sketch, "E34.top", {"start": v(25.4, -15.88) * mm, "end": v(22.23, -15.88) * mm});
            skLineSegment(sketch, "E34.left", {"start": v(25.4, 15.88) * mm, "end": v(25.4, -15.88) * mm});
            skLineSegment(sketch, "E34.right", {"start": v(22.23, 15.88) * mm, "end": v(22.23, -15.88) * mm});
            skLineSegment(sketch, "E35.bottom", {"start": v(9.52, 15.88) * mm, "end": v(6.35, 15.88) * mm});
            skLineSegment(sketch, "E35.top", {"start": v(9.53, -15.88) * mm, "end": v(6.35, -15.88) * mm});
            skLineSegment(sketch, "E35.left", {"start": v(9.52, 15.88) * mm, "end": v(9.53, -15.88) * mm});
            skLineSegment(sketch, "E35.right", {"start": v(6.35, 15.88) * mm, "end": v(6.35, -15.88) * mm});
            skLineSegment(sketch, "E36.bottom", {"start": v(-6.35, 15.88) * mm, "end": v(-9.52, 15.88) * mm});
            skLineSegment(sketch, "E36.top", {"start": v(-6.35, -15.88) * mm, "end": v(-9.52, -15.88) * mm});
            skLineSegment(sketch, "E36.left", {"start": v(-6.35, 15.88) * mm, "end": v(-6.35, -15.88) * mm});
            skLineSegment(sketch, "E36.right", {"start": v(-9.52, 15.88) * mm, "end": v(-9.52, -15.88) * mm});
            skLineSegment(sketch, "E37.bottom", {"start": v(-22.22, 15.88) * mm, "end": v(-25.4, 15.88) * mm});
            skLineSegment(sketch, "E37.top", {"start": v(-22.22, -15.88) * mm, "end": v(-25.4, -15.88) * mm});
            skLineSegment(sketch, "E37.left", {"start": v(-22.22, 15.88) * mm, "end": v(-22.22, -15.88) * mm});
            skLineSegment(sketch, "E37.right", {"start": v(-25.4, 15.88) * mm, "end": v(-25.4, -15.88) * mm});
            skLineSegment(sketch, "E38.bottom", {"start": v(-38.1, 15.88) * mm, "end": v(-41.27, 15.88) * mm});
            skLineSegment(sketch, "E38.top", {"start": v(-38.1, -15.88) * mm, "end": v(-41.27, -15.88) * mm});
            skLineSegment(sketch, "E38.left", {"start": v(-38.1, 15.88) * mm, "end": v(-38.1, -15.88) * mm});
            skLineSegment(sketch, "E38.right", {"start": v(-41.27, 15.88) * mm, "end": v(-41.27, -15.88) * mm});
            skLineSegment(sketch, "E39.bottom", {"start": v(-53.98, 15.88) * mm, "end": v(-57.15, 15.88) * mm});
            skLineSegment(sketch, "E39.top", {"start": v(-53.97, -15.88) * mm, "end": v(-57.15, -15.88) * mm});
            skLineSegment(sketch, "E39.left", {"start": v(-53.98, 15.88) * mm, "end": v(-53.97, -15.88) * mm});
            skLineSegment(sketch, "E39.right", {"start": v(-57.15, 15.88) * mm, "end": v(-57.15, -15.88) * mm});
            skLineSegment(sketch, "E40.bottom", {"start": v(-69.85, 15.88) * mm, "end": v(-73.02, 15.88) * mm});
            skLineSegment(sketch, "E40.top", {"start": v(-69.85, -15.88) * mm, "end": v(-73.02, -15.88) * mm});
            skLineSegment(sketch, "E40.left", {"start": v(-69.85, 15.88) * mm, "end": v(-69.85, -15.88) * mm});
            skLineSegment(sketch, "E40.right", {"start": v(-73.02, 15.88) * mm, "end": v(-73.02, -15.88) * mm});
            skLineSegment(sketch, "E41", {"start": v(-74.93, 15.88) * mm, "end": v(74.93, 15.88) * mm, "construction": true});
            skSolve(sketch);
        }
        {
            var Q0;
            Q0 = qSketchRegion(id + "F26", true);
            extrude(context, id + "F27", {"entities" : qUnion([Q0]), "operationType" : NewBodyOperationType.ADD, "depth" : 11.43 * mm});
        }
        {
            var Q0;
            Q0=makeQuery(id+"F27.opExtrude","CAP_EDGE",EDGE,{"disambiguationData":[OSD([sQuery(id+"F26.wireOp",EDGE,"E40.top")])],"isStart":false});
            var Q1;
            Q1=makeQuery(id+"F27.opExtrude","CAP_EDGE",EDGE,{"disambiguationData":[OSD([sQuery(id+"F26.wireOp",EDGE,"E39.top")])],"isStart":false});
            var Q2;
            Q2=makeQuery(id+"F27.opExtrude","CAP_EDGE",EDGE,{"disambiguationData":[OSD([sQuery(id+"F26.wireOp",EDGE,"E38.top")])],"isStart":false});
            var Q3;
            Q3=makeQuery(id+"F27.opExtrude","CAP_EDGE",EDGE,{"disambiguationData":[OSD([sQuery(id+"F26.wireOp",EDGE,"E37.top")])],"isStart":false});
            var Q4;
            Q4=makeQuery(id+"F27.opExtrude","CAP_EDGE",EDGE,{"disambiguationData":[OSD([sQuery(id+"F26.wireOp",EDGE,"E36.top")])],"isStart":false});
            var Q5;
            Q5=makeQuery(id+"F27.opExtrude","CAP_EDGE",EDGE,{"disambiguationData":[OSD([sQuery(id+"F26.wireOp",EDGE,"E35.top")])],"isStart":false});
            var Q6;
            Q6=makeQuery(id+"F27.opExtrude","CAP_EDGE",EDGE,{"disambiguationData":[OSD([sQuery(id+"F26.wireOp",EDGE,"E34.top")])],"isStart":false});
            var Q7;
            Q7=makeQuery(id+"F27.opExtrude","CAP_EDGE",EDGE,{"disambiguationData":[OSD([sQuery(id+"F26.wireOp",EDGE,"E33.top")])],"isStart":false});
            var Q8;
            Q8=makeQuery(id+"F27.opExtrude","CAP_EDGE",EDGE,{"disambiguationData":[OSD([sQuery(id+"F26.wireOp",EDGE,"E32.top")])],"isStart":false});
            var Q9;
            Q9=makeQuery(id+"F27.opExtrude","CAP_EDGE",EDGE,{"disambiguationData":[OSD([sQuery(id+"F26.wireOp",EDGE,"E31.top")])],"isStart":false});
            var Q10;
            Q10=makeQuery(id+"F27.opExtrude","CAP_EDGE",EDGE,{"disambiguationData":[OSD([sQuery(id+"F26.wireOp",EDGE,"E31.bottom")])],"isStart":false});
            var Q11;
            Q11=makeQuery(id+"F27.opExtrude","CAP_EDGE",EDGE,{"disambiguationData":[OSD([sQuery(id+"F26.wireOp",EDGE,"E32.bottom")])],"isStart":false});
            var Q12;
            Q12=makeQuery(id+"F27.opExtrude","CAP_EDGE",EDGE,{"disambiguationData":[OSD([sQuery(id+"F26.wireOp",EDGE,"E33.bottom")])],"isStart":false});
            var Q13;
            Q13=makeQuery(id+"F27.opExtrude","CAP_EDGE",EDGE,{"disambiguationData":[OSD([sQuery(id+"F26.wireOp",EDGE,"E34.bottom")])],"isStart":false});
            var Q14;
            Q14=makeQuery(id+"F27.opExtrude","CAP_EDGE",EDGE,{"disambiguationData":[OSD([sQuery(id+"F26.wireOp",EDGE,"E35.bottom")])],"isStart":false});
            var Q15;
            Q15=makeQuery(id+"F27.opExtrude","CAP_EDGE",EDGE,{"disambiguationData":[OSD([sQuery(id+"F26.wireOp",EDGE,"E36.bottom")])],"isStart":false});
            var Q16;
            Q16=makeQuery(id+"F27.opExtrude","CAP_EDGE",EDGE,{"disambiguationData":[OSD([sQuery(id+"F26.wireOp",EDGE,"E37.bottom")])],"isStart":false});
            var Q17;
            Q17=makeQuery(id+"F27.opExtrude","CAP_EDGE",EDGE,{"disambiguationData":[OSD([sQuery(id+"F26.wireOp",EDGE,"E38.bottom")])],"isStart":false});
            var Q18;
            Q18=makeQuery(id+"F27.opExtrude","CAP_EDGE",EDGE,{"disambiguationData":[OSD([sQuery(id+"F26.wireOp",EDGE,"E39.bottom")])],"isStart":false});
            var Q19;
            Q19=makeQuery(id+"F27.opExtrude","CAP_EDGE",EDGE,{"disambiguationData":[OSD([sQuery(id+"F26.wireOp",EDGE,"E40.bottom")])],"isStart":false});
            fillet(context, id + "F28", {"entities" : qUnion([Q0, Q1, Q2, Q3, Q4, Q5, Q6, Q7, Q8, Q9, Q10, Q11, Q12, Q13, Q14, Q15, Q16, Q17, Q18, Q19]), "radius" : 11.43 * mm, "tangentPropagation" : true, "allowEdgeOverflow" : false});
        }
        {
            var Q0;
            Q0=makeQuery(id+"F28.opFillet","BLEND_EDGE",EDGE,{"blendedFrom":[makeQuery(id+"F27.opExtrude","CAP_EDGE",EDGE,{"disambiguationData":[OSD([sQuery(id+"F26.wireOp",EDGE,"E40.top")])],"isStart":false}),makeQuery(id+"F6.opExtrude","CAP_FACE",FACE,{"disambiguationData":[OSD([sQuery(id+"F5.wireOp",EDGE,"E3.0"),sQuery(id+"F5.wireOp",EDGE,"E4.0"),sQuery(id+"F5.wireOp",EDGE,"E5.0"),sQuery(id+"F5.wireOp",EDGE,"E6.0")])],"isStart":false})],"blendedInto":[makeQuery(id+"F6.opExtrude","CAP_FACE",FACE,{"disambiguationData":[OSD([sQuery(id+"F5.wireOp",EDGE,"E3.0"),sQuery(id+"F5.wireOp",EDGE,"E4.0"),sQuery(id+"F5.wireOp",EDGE,"E5.0"),sQuery(id+"F5.wireOp",EDGE,"E6.0")])],"isStart":false})]});
            var Q1;
            Q1=makeQuery(id+"F28.opFillet","BLEND_EDGE",EDGE,{"blendedFrom":[makeQuery(id+"F27.opExtrude","CAP_EDGE",EDGE,{"disambiguationData":[OSD([sQuery(id+"F26.wireOp",EDGE,"E39.top")])],"isStart":false}),makeQuery(id+"F6.opExtrude","CAP_FACE",FACE,{"disambiguationData":[OSD([sQuery(id+"F5.wireOp",EDGE,"E3.0"),sQuery(id+"F5.wireOp",EDGE,"E4.0"),sQuery(id+"F5.wireOp",EDGE,"E5.0"),sQuery(id+"F5.wireOp",EDGE,"E6.0")])],"isStart":false})],"blendedInto":[makeQuery(id+"F6.opExtrude","CAP_FACE",FACE,{"disambiguationData":[OSD([sQuery(id+"F5.wireOp",EDGE,"E3.0"),sQuery(id+"F5.wireOp",EDGE,"E4.0"),sQuery(id+"F5.wireOp",EDGE,"E5.0"),sQuery(id+"F5.wireOp",EDGE,"E6.0")])],"isStart":false})]});
            var Q2;
            Q2=makeQuery(id+"F28.opFillet","BLEND_EDGE",EDGE,{"blendedFrom":[makeQuery(id+"F27.opExtrude","CAP_EDGE",EDGE,{"disambiguationData":[OSD([sQuery(id+"F26.wireOp",EDGE,"E38.top")])],"isStart":false}),makeQuery(id+"F6.opExtrude","CAP_FACE",FACE,{"disambiguationData":[OSD([sQuery(id+"F5.wireOp",EDGE,"E3.0"),sQuery(id+"F5.wireOp",EDGE,"E4.0"),sQuery(id+"F5.wireOp",EDGE,"E5.0"),sQuery(id+"F5.wireOp",EDGE,"E6.0")])],"isStart":false})],"blendedInto":[makeQuery(id+"F6.opExtrude","CAP_FACE",FACE,{"disambiguationData":[OSD([sQuery(id+"F5.wireOp",EDGE,"E3.0"),sQuery(id+"F5.wireOp",EDGE,"E4.0"),sQuery(id+"F5.wireOp",EDGE,"E5.0"),sQuery(id+"F5.wireOp",EDGE,"E6.0")])],"isStart":false})]});
            var Q3;
            Q3=makeQuery(id+"F28.opFillet","BLEND_EDGE",EDGE,{"blendedFrom":[makeQuery(id+"F27.opExtrude","CAP_EDGE",EDGE,{"disambiguationData":[OSD([sQuery(id+"F26.wireOp",EDGE,"E37.top")])],"isStart":false}),makeQuery(id+"F6.opExtrude","CAP_FACE",FACE,{"disambiguationData":[OSD([sQuery(id+"F5.wireOp",EDGE,"E3.0"),sQuery(id+"F5.wireOp",EDGE,"E4.0"),sQuery(id+"F5.wireOp",EDGE,"E5.0"),sQuery(id+"F5.wireOp",EDGE,"E6.0")])],"isStart":false})],"blendedInto":[makeQuery(id+"F6.opExtrude","CAP_FACE",FACE,{"disambiguationData":[OSD([sQuery(id+"F5.wireOp",EDGE,"E3.0"),sQuery(id+"F5.wireOp",EDGE,"E4.0"),sQuery(id+"F5.wireOp",EDGE,"E5.0"),sQuery(id+"F5.wireOp",EDGE,"E6.0")])],"isStart":false})]});
            var Q4;
            Q4=makeQuery(id+"F28.opFillet","BLEND_EDGE",EDGE,{"blendedFrom":[makeQuery(id+"F27.opExtrude","CAP_EDGE",EDGE,{"disambiguationData":[OSD([sQuery(id+"F26.wireOp",EDGE,"E36.top")])],"isStart":false}),makeQuery(id+"F6.opExtrude","CAP_FACE",FACE,{"disambiguationData":[OSD([sQuery(id+"F5.wireOp",EDGE,"E3.0"),sQuery(id+"F5.wireOp",EDGE,"E4.0"),sQuery(id+"F5.wireOp",EDGE,"E5.0"),sQuery(id+"F5.wireOp",EDGE,"E6.0")])],"isStart":false})],"blendedInto":[makeQuery(id+"F6.opExtrude","CAP_FACE",FACE,{"disambiguationData":[OSD([sQuery(id+"F5.wireOp",EDGE,"E3.0"),sQuery(id+"F5.wireOp",EDGE,"E4.0"),sQuery(id+"F5.wireOp",EDGE,"E5.0"),sQuery(id+"F5.wireOp",EDGE,"E6.0")])],"isStart":false})]});
            var Q5;
            Q5=makeQuery(id+"F28.opFillet","BLEND_EDGE",EDGE,{"blendedFrom":[makeQuery(id+"F27.opExtrude","CAP_EDGE",EDGE,{"disambiguationData":[OSD([sQuery(id+"F26.wireOp",EDGE,"E35.top")])],"isStart":false}),makeQuery(id+"F6.opExtrude","CAP_FACE",FACE,{"disambiguationData":[OSD([sQuery(id+"F5.wireOp",EDGE,"E3.0"),sQuery(id+"F5.wireOp",EDGE,"E4.0"),sQuery(id+"F5.wireOp",EDGE,"E5.0"),sQuery(id+"F5.wireOp",EDGE,"E6.0")])],"isStart":false})],"blendedInto":[makeQuery(id+"F6.opExtrude","CAP_FACE",FACE,{"disambiguationData":[OSD([sQuery(id+"F5.wireOp",EDGE,"E3.0"),sQuery(id+"F5.wireOp",EDGE,"E4.0"),sQuery(id+"F5.wireOp",EDGE,"E5.0"),sQuery(id+"F5.wireOp",EDGE,"E6.0")])],"isStart":false})]});
            var Q6;
            Q6=makeQuery(id+"F28.opFillet","BLEND_EDGE",EDGE,{"blendedFrom":[makeQuery(id+"F27.opExtrude","CAP_EDGE",EDGE,{"disambiguationData":[OSD([sQuery(id+"F26.wireOp",EDGE,"E34.top")])],"isStart":false}),makeQuery(id+"F6.opExtrude","CAP_FACE",FACE,{"disambiguationData":[OSD([sQuery(id+"F5.wireOp",EDGE,"E3.0"),sQuery(id+"F5.wireOp",EDGE,"E4.0"),sQuery(id+"F5.wireOp",EDGE,"E5.0"),sQuery(id+"F5.wireOp",EDGE,"E6.0")])],"isStart":false})],"blendedInto":[makeQuery(id+"F6.opExtrude","CAP_FACE",FACE,{"disambiguationData":[OSD([sQuery(id+"F5.wireOp",EDGE,"E3.0"),sQuery(id+"F5.wireOp",EDGE,"E4.0"),sQuery(id+"F5.wireOp",EDGE,"E5.0"),sQuery(id+"F5.wireOp",EDGE,"E6.0")])],"isStart":false})]});
            var Q7;
            Q7=makeQuery(id+"F28.opFillet","BLEND_EDGE",EDGE,{"blendedFrom":[makeQuery(id+"F27.opExtrude","CAP_EDGE",EDGE,{"disambiguationData":[OSD([sQuery(id+"F26.wireOp",EDGE,"E33.top")])],"isStart":false}),makeQuery(id+"F6.opExtrude","CAP_FACE",FACE,{"disambiguationData":[OSD([sQuery(id+"F5.wireOp",EDGE,"E3.0"),sQuery(id+"F5.wireOp",EDGE,"E4.0"),sQuery(id+"F5.wireOp",EDGE,"E5.0"),sQuery(id+"F5.wireOp",EDGE,"E6.0")])],"isStart":false})],"blendedInto":[makeQuery(id+"F6.opExtrude","CAP_FACE",FACE,{"disambiguationData":[OSD([sQuery(id+"F5.wireOp",EDGE,"E3.0"),sQuery(id+"F5.wireOp",EDGE,"E4.0"),sQuery(id+"F5.wireOp",EDGE,"E5.0"),sQuery(id+"F5.wireOp",EDGE,"E6.0")])],"isStart":false})]});
            var Q8;
            Q8=makeQuery(id+"F28.opFillet","BLEND_EDGE",EDGE,{"blendedFrom":[makeQuery(id+"F27.opExtrude","CAP_EDGE",EDGE,{"disambiguationData":[OSD([sQuery(id+"F26.wireOp",EDGE,"E32.top")])],"isStart":false}),makeQuery(id+"F6.opExtrude","CAP_FACE",FACE,{"disambiguationData":[OSD([sQuery(id+"F5.wireOp",EDGE,"E3.0"),sQuery(id+"F5.wireOp",EDGE,"E4.0"),sQuery(id+"F5.wireOp",EDGE,"E5.0"),sQuery(id+"F5.wireOp",EDGE,"E6.0")])],"isStart":false})],"blendedInto":[makeQuery(id+"F6.opExtrude","CAP_FACE",FACE,{"disambiguationData":[OSD([sQuery(id+"F5.wireOp",EDGE,"E3.0"),sQuery(id+"F5.wireOp",EDGE,"E4.0"),sQuery(id+"F5.wireOp",EDGE,"E5.0"),sQuery(id+"F5.wireOp",EDGE,"E6.0")])],"isStart":false})]});
            var Q9;
            Q9=makeQuery(id+"F28.opFillet","BLEND_EDGE",EDGE,{"blendedFrom":[makeQuery(id+"F27.opExtrude","CAP_EDGE",EDGE,{"disambiguationData":[OSD([sQuery(id+"F26.wireOp",EDGE,"E31.top")])],"isStart":false}),makeQuery(id+"F6.opExtrude","CAP_FACE",FACE,{"disambiguationData":[OSD([sQuery(id+"F5.wireOp",EDGE,"E3.0"),sQuery(id+"F5.wireOp",EDGE,"E4.0"),sQuery(id+"F5.wireOp",EDGE,"E5.0"),sQuery(id+"F5.wireOp",EDGE,"E6.0")])],"isStart":false})],"blendedInto":[makeQuery(id+"F6.opExtrude","CAP_FACE",FACE,{"disambiguationData":[OSD([sQuery(id+"F5.wireOp",EDGE,"E3.0"),sQuery(id+"F5.wireOp",EDGE,"E4.0"),sQuery(id+"F5.wireOp",EDGE,"E5.0"),sQuery(id+"F5.wireOp",EDGE,"E6.0")])],"isStart":false})]});
            var Q10;
            Q10=makeQuery(id+"F27.opExtrude","CAP_EDGE",EDGE,{"disambiguationData":[OSD([sQuery(id+"F26.wireOp",EDGE,"E31.right")])],"isStart":true});
            var Q11;
            Q11=makeQuery(id+"F27.opExtrude","CAP_EDGE",EDGE,{"disambiguationData":[OSD([sQuery(id+"F26.wireOp",EDGE,"E32.left")])],"isStart":true});
            var Q12;
            Q12=makeQuery(id+"F27.opExtrude","CAP_EDGE",EDGE,{"disambiguationData":[OSD([sQuery(id+"F26.wireOp",EDGE,"E33.left")])],"isStart":true});
            var Q13;
            Q13=makeQuery(id+"F27.opExtrude","CAP_EDGE",EDGE,{"disambiguationData":[OSD([sQuery(id+"F26.wireOp",EDGE,"E34.left")])],"isStart":true});
            var Q14;
            Q14=makeQuery(id+"F27.opExtrude","CAP_EDGE",EDGE,{"disambiguationData":[OSD([sQuery(id+"F26.wireOp",EDGE,"E35.left")])],"isStart":true});
            var Q15;
            Q15=makeQuery(id+"F27.opExtrude","CAP_EDGE",EDGE,{"disambiguationData":[OSD([sQuery(id+"F26.wireOp",EDGE,"E36.left")])],"isStart":true});
            var Q16;
            Q16=makeQuery(id+"F27.opExtrude","CAP_EDGE",EDGE,{"disambiguationData":[OSD([sQuery(id+"F26.wireOp",EDGE,"E37.left")])],"isStart":true});
            var Q17;
            Q17=makeQuery(id+"F27.opExtrude","CAP_EDGE",EDGE,{"disambiguationData":[OSD([sQuery(id+"F26.wireOp",EDGE,"E38.left")])],"isStart":true});
            var Q18;
            Q18=makeQuery(id+"F27.opExtrude","CAP_EDGE",EDGE,{"disambiguationData":[OSD([sQuery(id+"F26.wireOp",EDGE,"E39.left")])],"isStart":true});
            var Q19;
            Q19=makeQuery(id+"F27.opExtrude","CAP_EDGE",EDGE,{"disambiguationData":[OSD([sQuery(id+"F26.wireOp",EDGE,"E39.left")])],"isStart":false});
            var Q20;
            Q20=makeQuery(id+"F27.opExtrude","CAP_EDGE",EDGE,{"disambiguationData":[OSD([sQuery(id+"F26.wireOp",EDGE,"E38.left")])],"isStart":false});
            var Q21;
            Q21=makeQuery(id+"F27.opExtrude","CAP_EDGE",EDGE,{"disambiguationData":[OSD([sQuery(id+"F26.wireOp",EDGE,"E37.left")])],"isStart":false});
            var Q22;
            Q22=makeQuery(id+"F27.opExtrude","CAP_EDGE",EDGE,{"disambiguationData":[OSD([sQuery(id+"F26.wireOp",EDGE,"E36.left")])],"isStart":false});
            var Q23;
            Q23=makeQuery(id+"F27.opExtrude","CAP_EDGE",EDGE,{"disambiguationData":[OSD([sQuery(id+"F26.wireOp",EDGE,"E35.left")])],"isStart":false});
            var Q24;
            Q24=makeQuery(id+"F27.opExtrude","CAP_EDGE",EDGE,{"disambiguationData":[OSD([sQuery(id+"F26.wireOp",EDGE,"E34.left")])],"isStart":false});
            var Q25;
            Q25=makeQuery(id+"F27.opExtrude","CAP_EDGE",EDGE,{"disambiguationData":[OSD([sQuery(id+"F26.wireOp",EDGE,"E33.left")])],"isStart":false});
            var Q26;
            Q26=makeQuery(id+"F27.opExtrude","CAP_EDGE",EDGE,{"disambiguationData":[OSD([sQuery(id+"F26.wireOp",EDGE,"E32.left")])],"isStart":false});
            var Q27;
            Q27=makeQuery(id+"F27.opExtrude","CAP_EDGE",EDGE,{"disambiguationData":[OSD([sQuery(id+"F26.wireOp",EDGE,"E31.right")])],"isStart":false});
            var Q28;
            Q28=makeQuery(id+"F27.opExtrude","CAP_EDGE",EDGE,{"disambiguationData":[OSD([sQuery(id+"F26.wireOp",EDGE,"E40.left")])],"isStart":false});
            var Q29;
            Q29=makeQuery(id+"F27.opExtrude","CAP_EDGE",EDGE,{"disambiguationData":[OSD([sQuery(id+"F26.wireOp",EDGE,"E40.right")])],"isStart":false});
            var Q30;
            Q30=makeQuery(id+"F27.opExtrude","CAP_EDGE",EDGE,{"disambiguationData":[OSD([sQuery(id+"F26.wireOp",EDGE,"E39.right")])],"isStart":false});
            var Q31;
            Q31=makeQuery(id+"F27.opExtrude","CAP_EDGE",EDGE,{"disambiguationData":[OSD([sQuery(id+"F26.wireOp",EDGE,"E38.right")])],"isStart":false});
            var Q32;
            Q32=makeQuery(id+"F27.opExtrude","CAP_EDGE",EDGE,{"disambiguationData":[OSD([sQuery(id+"F26.wireOp",EDGE,"E37.right")])],"isStart":false});
            var Q33;
            Q33=makeQuery(id+"F27.opExtrude","CAP_EDGE",EDGE,{"disambiguationData":[OSD([sQuery(id+"F26.wireOp",EDGE,"E36.right")])],"isStart":false});
            var Q34;
            Q34=makeQuery(id+"F27.opExtrude","CAP_EDGE",EDGE,{"disambiguationData":[OSD([sQuery(id+"F26.wireOp",EDGE,"E35.right")])],"isStart":false});
            var Q35;
            Q35=makeQuery(id+"F27.opExtrude","CAP_EDGE",EDGE,{"disambiguationData":[OSD([sQuery(id+"F26.wireOp",EDGE,"E34.right")])],"isStart":false});
            var Q36;
            Q36=makeQuery(id+"F27.opExtrude","CAP_EDGE",EDGE,{"disambiguationData":[OSD([sQuery(id+"F26.wireOp",EDGE,"E33.right")])],"isStart":false});
            var Q37;
            Q37=makeQuery(id+"F27.opExtrude","CAP_EDGE",EDGE,{"disambiguationData":[OSD([sQuery(id+"F26.wireOp",EDGE,"E32.right")])],"isStart":false});
            var Q38;
            Q38=makeQuery(id+"F27.opExtrude","CAP_EDGE",EDGE,{"disambiguationData":[OSD([sQuery(id+"F26.wireOp",EDGE,"E31.left")])],"isStart":false});
            var Q39;
            Q39=makeQuery(id+"F27.opExtrude","CAP_EDGE",EDGE,{"disambiguationData":[OSD([sQuery(id+"F26.wireOp",EDGE,"E40.left")])],"isStart":true});
            fillet(context, id + "F29", {"entities" : qUnion([Q0, Q1, Q2, Q3, Q4, Q5, Q6, Q7, Q8, Q9, Q10, Q11, Q12, Q13, Q14, Q15, Q16, Q17, Q18, Q19, Q20, Q21, Q22, Q23, Q24, Q25, Q26, Q27, Q28, Q29, Q30, Q31, Q32, Q33, Q34, Q35, Q36, Q37, Q38, Q39]), "radius" : 1.27 * mm, "tangentPropagation" : true, "allowEdgeOverflow" : false});
        }
    });
